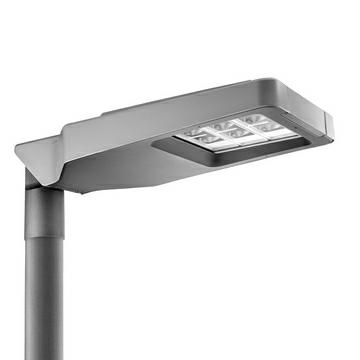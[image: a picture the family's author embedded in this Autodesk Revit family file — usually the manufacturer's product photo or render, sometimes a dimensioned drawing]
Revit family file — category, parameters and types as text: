
# Revit family: Lighting-StreetLighting-GEWISS-ROAD[5]MINI-LED_OPTIC_WIDE_CLII
name_source: partatom
category: Apparecchi per illuminazione
units: mm (PartAtom-declared; Revit-internal decimal feet)

## family parameters
Basato su piano di lavoro = No
Condiviso = No
Punto di calcolo locali = No
Quota connettore circolare = Usa diametro
Sempre verticale = Sì
Sorgente d'illuminazione = No
Taglio con vuoti quando caricato = No
Tipo di parte = Normale

## types (44) — shared parameters
Applicazione = External
Carico apparente = 53 VA
Catalogue = LIGHTING
Commenti sul wattaggio = 53W
IDF = 1914d6a6-8cfd-45a9-bf41-70975823a003
IDT = 3cb2f9b43b7a40689a44ddfc6caf9e96
IP degree = IP66
Immagine tipo = GWR5276M.jpg
Insulation class = II
Produttore = GEWISS S.p.A.
Shock resistance = IK08
Technical sheet = https://www.gewiss.com
URL = https://www.gewiss.com
Version file RFA = 20.11
Warranty = 5 years

## per-type parameters (varying)
- GWR5212V - ROAD5 MINI V.WIDE 2M 4000K 1,0A CL2: Body=Die-cast aluminium -; Catalogue Range=ROAD [5]; Classification:=-; Color Rendering Index=CRI-70; Colore=Graphite grey; Colour :=Powder coating; Colour temperature=4000K; Colour temperature:=4000 K (CRI>70); Context=Street and parking lighting; Control System=DALI - 5 Step; DIN 18032-3 certification=-; Descrizione=GWR5212V - ROAD5 MINI V.WIDE 2M 4000K 1,0A CL2; Device with reduced surface temperature=-; Driver=Included; Driver Box=Built-in; Efficiency (lm/W)=110; Electrocod=244C; Eletrical and lighting features=-; External screw=Stainless steel; Fixing=Pole Head - Outreach; Gasket=Anti-aging silicone; General information=-; Glow Wire Test :=-; IPEA=ROAD = A3 + // LARGE AREAS = A4 + // CYCLOPEDONALS = A ++ // GREEN AREAS = A ++ // HISTORICAL CENTER = A6 +; Installationa and maintenance=-; LED Life Time (L80B05)=120000H; LED Maintenance=Not available; LED current.=1A; Lamp-=LED; Lifetime=L90B10 (Tq+25°C) = 100.000 h - L90B10 (Tq+40°C) = 75.000 h; Locking Hook=Integrated front handle; Lumen output (lm)=8500; Luminaire=LED Road Equipment; Materials=-; Maximum surface exposed to the wind=0,149999999999999M2; Maximum surface exposed to the wind :=0.15 m²; Minimum distance from the illuminated object=1M; Modello=GWR5212V; Mouting and installation=Pole Head - Outreach; Nominal flux (lm)=9540; Number of modules=2 (2x3 LED); Operating temperature :=-25 +40 °C; Operating temperature:=-25 +40 °C; Optic=WIDE; Optic :=Metallized polycarbonate reflector; Optic Maintenance=Not available; Optic and illuminating features=-; Overvoltage protection=DM 10KV / CM 10KV; Photobiological Risk Class=RG0; Rated frequency (Hz)=50 / 60; SEO=Street lighting; Shield type=4mm thick flat tempered glass; Standard Deviation Colour Matching=SDCM = 5; Standard-=EN 60598-2-3, EN 60598-1 IEC/TR 62778; Standards and approvals=-; Stocking temperature=-; Supply voltage=220 - 240 V; System power=76W; System power :=77 W @ 1A; Tilt adjustable=-20° ÷ +10° side bracket - -10° ÷ +20° pole head; Tilt-=-20° ÷ +10° side bracket - -10° ÷ +20° pole head; Tipologia=Programmable (5 step); Type of light source=LED - Not replaceable; Unified Glare Rating=G*3 - ULOR = 0; Unique digital code (Datamatrix)=Currently not present; Voltage-=220/240 V - 50/60 Hz - Stand alone and/or programmable; Weight (kg):=6,6; Wiring=Isolating switch
- GWR5212B - ROAD 5 MINI BIPOW.2M 4000K 1A OPT.W: Catalogue Range=ROAD [5]; Colour temperature=4000 K (CRI 70); Colour temperature:=4000 K (CRI 70); Descrizione=ROAD 5 MINI BIPOW.2M 4000K 1A OPT.W; EAN code=8011564857872; Electrocod=244C; LED LifeTime (L80B05)=120000H; LED current.=1A; Lamp-=LED; Lumen output (lm)=7680; Maximum surface exposed to the wind=0,15M2; Minimum distance from the illuminated object=1M; Modello=GWR5212B; No. Chorus modules=2 (2x3 LED); Nominal flux (lm)=9540; Number of modules=2 (2x3 LED); Operating temperature:=-25 +40 °C; Optic=W - ULOR: 0%; Overvoltage resistance=12 KV (Common and dfferential mode); Pilot current=1A; Power supply operation=Bi power; SEO=Street lighting; System power=77W; Tilt adjustable=-20° ÷ +10° side bracket - -10° ÷ +20° pole head; Tipo alimentatore=Constant Current Driver Led; Tipologia=Bi power; Type of lamp=LED; Voltage-=220/240 V - 50/60 Hz - Bi-power with self-learning; Weight (kg)=6,6; Weight (kg):=6,6; Working temperature=-25 +40 °C
- GWR523130K - ROAD 5 MINI ST.AL.1M 3000K 350mA OPT.W: Body=Die-cast aluminium -; Catalogue Range=ROAD [5]; Classification:=-; Color Rendering Index=CRI-70; Colore=Graphite grey; Colour :=Powder coating; Colour temperature=3000K; Colour temperature:=3000 K (CRI>80); Context=Street and parking lighting; Control System=Stand alone; DIN 18032-3 certification=-; Descrizione=GWR523130K - ROAD 5 MINI ST.AL.1M 3000K 350mA OPT.W; Device with reduced surface temperature=-; Driver=Included; Driver Box=Built-in; Efficiency (lm/W)=115; Electrocod=244C; Eletrical and lighting features=-; External screw=Stainless steel; Fixing=Pole Head - Outreach; Gasket=Anti-aging silicone; General information=-; Glow Wire Test :=-; IPEA=ROAD = A4 + // LARGE AREAS = A5 + // CYCLOPEDONALS = A4 + // GREEN AREAS = A4 + // HISTORICAL CENTER = A6 +; Installationa and maintenance=-; LED Life Time (L80B05)=77000H; LED Maintenance=Not available; LED current.=0,35A; Lamp-=LED; Lifetime=L90B10 (Tq+25°C) = 100.000 h - L90B10 (Tq+50°C) = 75.000 h; Locking Hook=Integrated front handle; Lumen output (lm)=1500; Luminaire=LED Road Equipment; Materials=-; Maximum surface exposed to the wind=0,149999999999999M2; Maximum surface exposed to the wind :=0.15 m²; Minimum distance from the illuminated object=1M; Modello=GWR523130K; Mouting and installation=Pole Head - Outreach; Nominal flux (lm)=1350; Number of modules=1 (1x3 LED); Operating temperature :=-25 +50 °C; Operating temperature:=-25 +50 °C; Optic=WIDE; Optic :=Metallized polycarbonate reflector; Optic Maintenance=Not available; Optic and illuminating features=-; Overvoltage protection=DM 10KV / CM 10KV; Overvoltage resistance :=Common and dfferential mode: 10KV; Photobiological Risk Class=RG0; Rated frequency (Hz)=50 / 60; SEO=Street lighting; Shield type=4mm thick flat tempered glass; Standard Deviation Colour Matching=SDCM = 5; Standard-=EN 60598-2-3, EN 60598-1 IEC/TR 62778; Standards and approvals=-; Stocking temperature=-; Supply voltage=220 - 240 V; System power=14W; System power :=13 W @ 0.35A; Tilt adjustable=-20° ÷ +10° side bracket - -10° ÷ +20° pole head; Tilt-=-20° ÷ +10° side bracket - -10° ÷ +20° pole head; Tipo alimentatore=Constant Current Driver Led; Tipologia=Stand alone; Type of light source=LED - Not replaceable; Unified Glare Rating=G*3 - ULOR = 0; Unique digital code (Datamatrix)=Currently not present; Voltage-=220/240 V - 50/60 Hz - Stand alone; Weight (kg):=6,4; Wiring=Isolating switch
- GWR5212V30K - ROAD 5 MINI DIMM.2M 3000K 1A OPT.W: Body=Die-cast aluminium -; Classification:=-; Color Rendering Index=CRI-70; Colore=Graphite grey; Colour :=Powder coating; Colour temperature=3000K; Context=Street and parking lighting; Control System=DALI - 5 Step; DIN 18032-3 certification=-; Descrizione=GWR5212V30K - ROAD 5 MINI DIMM.2M 3000K 1A OPT.W; Device with reduced surface temperature=-; Driver=Included; Driver Box=Built-in; Efficiency (lm/W)=96; Eletrical and lighting features=-; External screw=Stainless steel; Fixing=Pole Head - Outreach; Gasket=Anti-aging silicone; General information=-; Glow Wire Test :=-; IPEA=ROAD = A + // LARGE AREAS = A ++ // CYCLOPEDONALS = A + // GREEN AREAS = A + // HISTORICAL CENTER = A5 +; Installationa and maintenance=-; LED Maintenance=Not available; Lifetime=L90B10 (Tq+25°C) = 100.000 h - L90B10 (Tq+40°C) = 75.000 h; Locking Hook=Integrated front handle; Lumen output (lm)=7400; Luminaire=LED Road Equipment; Materials=-; Maximum surface exposed to the wind :=0.15 m²; Modello=GWR5212V30K; Mouting and installation=Pole Head - Outreach; Number of modules=2 (2x3 LED); Operating temperature :=-25 +40 °C; Optic=WIDE; Optic :=Metallized polycarbonate reflector; Optic Maintenance=Not available; Optic and illuminating features=-; Overvoltage protection=DM 10KV / CM 10KV; Photobiological Risk Class=RG0; Rated frequency (Hz)=50 / 60; SEO=Street lighting; Shield type=4mm thick flat tempered glass; Standard Deviation Colour Matching=SDCM = 5; Standard-=EN 60598-2-3, EN 60598-1 IEC/TR 62778; Standards and approvals=-; Stocking temperature=-; Supply voltage=220 - 240 V; System power :=77 W @ 1A; Tilt-=-20° ÷ +10° side bracket - -10° ÷ +20° pole head; Type of light source=LED - Not replaceable; Unified Glare Rating=G*3 - ULOR = 0; Unique digital code (Datamatrix)=Currently not present; Weight (kg):=6,59999999999999; Wiring=Isolating switch
- GWR5271M30K - ROAD5 MINI WIDE 1M 3000K 0,7A CL2 1-10V: Body=Die-cast aluminium -; Catalogue Range=ROAD [5]; Classification:=-; Color Rendering Index=CRI-70; Colore=Graphite grey; Colour :=Powder coating; Colour temperature=3000K; Colour temperature:=3000 K (CRI>80); Context=Street and parking lighting; Control System=Dimmable 1-10 V; DIN 18032-3 certification=-; Descrizione=GWR5271M30K - ROAD5 MINI WIDE 1M 3000K 0,7A CL2 1-10V; Device with reduced surface temperature=-; Driver=Included; Driver Box=Built-in; Efficiency (lm/W)=100; Electrocod=244C; Eletrical and lighting features=-; External screw=Stainless steel; Fixing=Pole Head - Outreach; Gasket=Anti-aging silicone; General information=-; Glow Wire Test :=-; IPEA=ROAD = A ++ // LARGE AREAS = A3 + // CYCLOPEDONALS = A ++ // GREEN AREAS = A ++ // HISTORICAL CENTER = A5 +; Installationa and maintenance=-; LED Life Time (L80B05)=77000H; LED Maintenance=Not available; LED current.=0,7A; Lamp-=LED; Lifetime=L90B10 (Tq+25°C) = 100.000 h - L90B10 (Tq+50°C) = 75.000 h; Locking Hook=Integrated front handle; Lumen output (lm)=2800; Luminaire=LED Road Equipment; Materials=-; Maximum surface exposed to the wind=0,149999999999999M2; Maximum surface exposed to the wind :=0.15 m²; Minimum distance from the illuminated object=1M; Modello=GWR5271M30K; Mouting and installation=Pole Head - Outreach; Nominal flux (lm)=2700; Number of modules=1 (1x3 LED); Operating temperature :=-25 +50 °C; Operating temperature:=-25 +50 °C; Optic=WIDE; Optic :=Metallized polycarbonate reflector; Optic Maintenance=Not available; Optic and illuminating features=-; Overvoltage protection=DM 10KV / CM 10KV; Overvoltage resistance :=Common and dfferential mode: 10KV; Photobiological Risk Class=RG0; Power supply operation=Dimmable; Rated frequency (Hz)=50 / 60; SEO=Street lighting; Shield type=4mm thick flat tempered glass; Standard Deviation Colour Matching=SDCM = 5; Standard-=EN 60598-2-3, EN 60598-1 IEC/TR 62778; Standards and approvals=-; Stocking temperature=-; Supply voltage=220 - 240 V; System power=27W; System power :=28 W @ 0.7A; Tilt adjustable=-20° ÷ +10° side bracket - -10° ÷ +20° pole head; Tilt-=-20° ÷ +10° side bracket - -10° ÷ +20° pole head; Tipo alimentatore=Constant Current Driver Led; Tipologia=Dimmable; Type of light source=LED - Not replaceable; Unified Glare Rating=G*3 - ULOR = 0; Unique digital code (Datamatrix)=Currently not present; Voltage-=220/240 V - 50/60 Hz - Dimmable 1-10 V; Weight (kg):=6,4; Wiring=Isolating switch
- GWR5231 - ROAD 5 MINI ST.AL.1M 4000K 350mA OPT.W: Catalogue Range=ROAD [5]; Colour temperature=4000 K (CRI 70); Colour temperature:=4000 K (CRI 70); Descrizione=ROAD 5 MINI ST.AL.1M 4000K 350mA OPT.W; EAN code=8011564870222; Electrocod=244C; LED LifeTime (L80B05)=77000H; LED current.=0,35A; Lamp-=LED; Lumen output (lm)=1310; Maximum surface exposed to the wind=0,15M2; Minimum distance from the illuminated object=1M; Modello=GWR5231; No. Chorus modules=1 (1x3 LED); Nominal flux (lm)=1560; Number of modules=1 (1x3 LED); Operating temperature:=-25 +50 °C; Optic=W - ULOR: 0%; Overvoltage resistance=12 KV (Common and dfferential mode); Pilot current=0,35A; SEO=Street lighting; System power=14W; Tilt adjustable=-20° ÷ +10° side bracket - -10° ÷ +20° pole head; Tipo alimentatore=Constant Current Driver Led; Tipologia=Stand alone; Type of lamp=LED; Voltage-=220/240 V - 50/60 Hz - Stand alone; Weight (kg)=6,4; Weight (kg):=6,4; Working temperature=-25 +50 °C
- GWR5272B30K - ROAD5 MINI WIDE 2M 3000K 0,7A CL2 BIREG: Body=Die-cast aluminium -; Catalogue Range=ROAD [5]; Classification:=-; Color Rendering Index=CRI-70; Colore=Graphite grey; Colour :=Powder coating; Colour temperature=3000K; Colour temperature:=3000 K (CRI>80); Context=Street and parking lighting; Control System=Bi-power with self-learning; DIN 18032-3 certification=-; Descrizione=GWR5272B30K - ROAD5 MINI WIDE 2M 3000K 0,7A CL2 BIREG; Device with reduced surface temperature=-; Driver=Included; Driver Box=Built-in; Efficiency (lm/W)=102; Electrocod=244C; Eletrical and lighting features=-; External screw=Stainless steel; Fixing=Pole Head - Outreach; Gasket=Anti-aging silicone; General information=-; Glow Wire Test :=-; IPEA=ROAD = A ++ // LARGE AREAS = A3 + // CYCLOPEDONALS = A ++ // GREEN AREAS = A ++ // HISTORICAL CENTER = A5 +; Installationa and maintenance=-; LED Life Time (L80B05)=77000H; LED Maintenance=Not available; LED current.=0,7A; Lamp-=LED; Lifetime=L90B10 (Tq+25°C) = 100.000 h - L90B10 (Tq+50°C) = 75.000 h; Locking Hook=Integrated front handle; Lumen output (lm)=5500; Luminaire=LED Road Equipment; Materials=-; Maximum surface exposed to the wind=0,149999999999999M2; Maximum surface exposed to the wind :=0.15 m²; Minimum distance from the illuminated object=1M; Modello=GWR5272B30K; Mouting and installation=Pole Head - Outreach; Nominal flux (lm)=5400; Number of modules=2 (2x3 LED); Operating temperature :=-25 +50 °C; Operating temperature:=-25 +50 °C; Optic=WIDE; Optic :=Metallized polycarbonate reflector; Optic Maintenance=Not available; Optic and illuminating features=-; Overvoltage protection=DM 10KV / CM 10KV; Overvoltage resistance :=Common and dfferential mode: 10KV; Photobiological Risk Class=RG0; Power supply operation=Bi power; Rated frequency (Hz)=50 / 60; SEO=Street lighting; Shield type=4mm thick flat tempered glass; Standard Deviation Colour Matching=SDCM = 5; Standard-=EN 60598-2-3, EN 60598-1 IEC/TR 62778; Standards and approvals=-; Stocking temperature=-; Supply voltage=220 - 240 V; System power=54W; System power :=54 W @ 0.7A; Tilt adjustable=-20° ÷ +10° side bracket - -10° ÷ +20° pole head; Tilt-=-20° ÷ +10° side bracket - -10° ÷ +20° pole head; Tipo alimentatore=Constant Current Driver Led; Tipologia=Bi power; Type of light source=LED - Not replaceable; Unified Glare Rating=G*3 - ULOR = 0; Unique digital code (Datamatrix)=Currently not present; Voltage-=220/240 V - 50/60 Hz - Bi-power with self-learning; Weight (kg):=6,6; Wiring=Isolating switch
- GWR527230K - ROAD 5 MINI ST.AL.2M 3000K 700mA OPT.W: Body=Die-cast aluminium -; Catalogue Range=ROAD [5]; Classification:=-; Color Rendering Index=CRI-70; Colore=Graphite grey; Colour :=Powder coating; Colour temperature=3000K; Colour temperature:=3000 K (CRI>80); Context=Street and parking lighting; Control System=Stand alone; DIN 18032-3 certification=-; Descrizione=GWR527230K - ROAD 5 MINI ST.AL.2M 3000K 700mA OPT.W; Device with reduced surface temperature=-; Driver=Included; Driver Box=Built-in; Efficiency (lm/W)=104; Electrocod=244C; Eletrical and lighting features=-; External screw=Stainless steel; Fixing=Pole Head - Outreach; Gasket=Anti-aging silicone; General information=-; Glow Wire Test :=-; IPEA=ROAD = A3 + // LARGE AREAS = A3 + // CYCLOPEDONALS = A ++ // GREEN AREAS = A ++ // HISTORICAL CENTER = A6 +; Installationa and maintenance=-; LED Life Time (L80B05)=77000H; LED Maintenance=Not available; LED current.=0,7A; Lamp-=LED; Lifetime=L90B10 (Tq+25°C) = 100.000 h - L90B10 (Tq+50°C) = 75.000 h; Locking Hook=Integrated front handle; Lumen output (lm)=5500; Luminaire=LED Road Equipment; Materials=-; Maximum surface exposed to the wind=0,149999999999999M2; Maximum surface exposed to the wind :=0.15 m²; Minimum distance from the illuminated object=1M; Modello=GWR527230K; Mouting and installation=Pole Head - Outreach; Nominal flux (lm)=5400; Number of modules=2 (2x3 LED); Operating temperature :=-25 +50 °C; Operating temperature:=-25 +50 °C; Optic=WIDE; Optic :=Metallized polycarbonate reflector; Optic Maintenance=Not available; Optic and illuminating features=-; Overvoltage protection=DM 10KV / CM 10KV; Overvoltage resistance :=Common and dfferential mode: 10KV; Photobiological Risk Class=RG0; Rated frequency (Hz)=50 / 60; SEO=Street lighting; Shield type=4mm thick flat tempered glass; Standard Deviation Colour Matching=SDCM = 5; Standard-=EN 60598-2-3, EN 60598-1 IEC/TR 62778; Standards and approvals=-; Stocking temperature=-; Supply voltage=220 - 240 V; System power=53W; System power :=53 W @ 0.7A; Tilt adjustable=-20° ÷ +10° side bracket - -10° ÷ +20° pole head; Tilt-=-20° ÷ +10° side bracket - -10° ÷ +20° pole head; Tipo alimentatore=Constant Current Driver Led; Tipologia=Stand alone; Type of light source=LED - Not replaceable; Unified Glare Rating=G*3 - ULOR = 0; Unique digital code (Datamatrix)=Currently not present; Voltage-=220/240 V - 50/60 Hz - Stand alone; Weight (kg):=6,6; Wiring=Isolating switch
- GWR5252M30K - ROAD5 MINI WIDE 2M 3000K 0,50A CL2: Body=Die-cast aluminium -; Classification:=-; Color Rendering Index=CRI-70; Colore=Graphite grey; Colour :=Powder coating; Colour temperature=3000K; Context=Street and parking lighting; Control System=Dimmable 1-10 V; DIN 18032-3 certification=-; Descrizione=GWR5252M30K - ROAD5 MINI WIDE 2M 3000K 0,50A CL2; Device with reduced surface temperature=-; Driver=Included; Driver Box=Built-in; Efficiency (lm/W)=108; Eletrical and lighting features=-; External screw=Stainless steel; Fixing=Pole Head - Outreach; Gasket=Anti-aging silicone; General information=-; Glow Wire Test :=-; IPEA=ROAD = A3 + // LARGE AREAS = A4 + // CYCLOPEDONALS = A3 + // GREEN AREAS = A3 + // HISTORICAL CENTER = A6 +; Installationa and maintenance=-; LED Maintenance=Not available; Lifetime=L90B10 (Tq+25°C) = 100.000 h - L90B10 (Tq+50°C) = 75.000 h; Locking Hook=Integrated front handle; Lumen output (lm)=4100; Luminaire=LED Road Equipment; Materials=-; Maximum surface exposed to the wind :=0.15 m²; Modello=GWR5252M30K; Mouting and installation=Pole Head - Outreach; Number of modules=2 (2x3 LED); Operating temperature :=-25 +50 °C; Optic=WIDE; Optic :=Metallized polycarbonate reflector; Optic Maintenance=Not available; Optic and illuminating features=-; Overvoltage protection=DM 10KV / CM 10KV; Photobiological Risk Class=RG0; Rated frequency (Hz)=50 / 60; SEO=Street lighting; Shield type=4mm thick flat tempered glass; Standard Deviation Colour Matching=SDCM = 5; Standard-=EN 60598-2-3, EN 60598-1 IEC/TR 62778; Standards and approvals=-; Stocking temperature=-; Supply voltage=220 - 240 V; System power :=38 W @ 0.5A; Tilt-=-20° ÷ +10° side bracket - -10° ÷ +20° pole head; Type of light source=LED - Not replaceable; Unified Glare Rating=G*3 - ULOR = 0; Unique digital code (Datamatrix)=Currently not present; Weight (kg):=6,59999999999999; Wiring=Isolating switch
- GWR5251D30K - ROAD5 MINI WIDE 1M 3000K 0,5A CL2 DALI: Body=Die-cast aluminium -; Classification:=-; Color Rendering Index=CRI-70; Colore=Graphite grey; Colour :=Powder coating; Colour temperature=3000K; Context=Street and parking lighting; Control System=DALI; DIN 18032-3 certification=-; Descrizione=GWR5251D30K - ROAD5 MINI WIDE 1M 3000K 0,5A CL2 DALI; Device with reduced surface temperature=-; Driver=Included; Driver Box=Built-in; Efficiency (lm/W)=105; Eletrical and lighting features=-; External screw=Stainless steel; Fixing=Pole Head - Outreach; Gasket=Anti-aging silicone; General information=-; Glow Wire Test :=-; IPEA=ROAD = A3 + // LARGE AREAS = A3 + // CYCLOPEDONALS = A3 + // GREEN AREAS = A3 + // HISTORICAL CENTER = A6 +; Installationa and maintenance=-; LED Maintenance=Not available; Lifetime=L90B10 (Tq+25°C) = 100.000 h - L90B10 (Tq+50°C) = 75.000 h; Locking Hook=Integrated front handle; Lumen output (lm)=2100; Luminaire=LED Road Equipment; Materials=-; Maximum surface exposed to the wind :=0.15 m²; Modello=GWR5251D30K; Mouting and installation=Pole Head - Outreach; Number of modules=1 (1x3 LED); Operating temperature :=-25 +50 °C; Optic=WIDE; Optic :=Metallized polycarbonate reflector; Optic Maintenance=Not available; Optic and illuminating features=-; Overvoltage protection=DM 10KV / CM 10KV; Photobiological Risk Class=RG0; Rated frequency (Hz)=50 / 60; Shield type=4mm thick flat tempered glass; Standard Deviation Colour Matching=SDCM = 5; Standard-=EN 60598-2-3, EN 60598-1 IEC/TR 62778; Standards and approvals=-; Stocking temperature=-; Supply voltage=220 - 240 V; System power :=20 W @ 0.5A; Tilt-=-20° ÷ +10° side bracket - -10° ÷ +20° pole head; Type of light source=LED - Not replaceable; Unified Glare Rating=G*3 - ULOR = 0; Unique digital code (Datamatrix)=Currently not present; Weight (kg):=6,4; Wiring=Isolating switch
- GWR5231V - ROAD5 MINI V.WIDE 1M 4000K 0,35A CL2: Body=Die-cast aluminium -; Catalogue Range=ROAD [5]; Classification:=-; Color Rendering Index=CRI-70; Colore=Graphite grey; Colour :=Powder coating; Colour temperature=4000K; Colour temperature:=4000 K (CRI>70); Context=Street and parking lighting; Control System=DALI - 5 Step; DIN 18032-3 certification=-; Descrizione=GWR5231V - ROAD5 MINI V.WIDE 1M 4000K 0,35A CL2; Device with reduced surface temperature=-; Driver=Included; Driver Box=Built-in; Efficiency (lm/W)=121; Electrocod=244C; Eletrical and lighting features=-; External screw=Stainless steel; Fixing=Pole Head - Outreach; Gasket=Anti-aging silicone; General information=-; Glow Wire Test :=-; IPEA=ROAD = A5 + // LARGE AREAS = A6 + // CYCLOPEDONALS = A5 + // GREEN AREAS = A5 + // HISTORICAL CENTER = A6 +; Installationa and maintenance=-; LED Life Time (L80B05)=120000H; LED Maintenance=Not available; LED current.=0,35A; Lamp-=LED; Lifetime=L90B10 (Tq+25°C) = 100.000 h - L90B10 (Tq+50°C) = 75.000 h; Locking Hook=Integrated front handle; Lumen output (lm)=1700; Luminaire=LED Road Equipment; Materials=-; Maximum surface exposed to the wind=0,149999999999999M2; Maximum surface exposed to the wind :=0.15 m²; Minimum distance from the illuminated object=1M; Modello=GWR5231V; Mouting and installation=Pole Head - Outreach; Nominal flux (lm)=1560; Number of modules=1 (1x3 LED); Operating temperature :=-25 +50 °C; Operating temperature:=-25 +40 °C; Optic=WIDE; Optic :=Metallized polycarbonate reflector; Optic Maintenance=Not available; Optic and illuminating features=-; Overvoltage protection=DM 10KV / CM 10KV; Photobiological Risk Class=RG0; Rated frequency (Hz)=50 / 60; SEO=Street lighting; Shield type=4mm thick flat tempered glass; Standard Deviation Colour Matching=SDCM = 5; Standard-=EN 60598-2-3, EN 60598-1 IEC/TR 62778; Standards and approvals=-; Stocking temperature=-; Supply voltage=220 - 240 V; System power=14W; System power :=14 W @ 0.35A; Tilt adjustable=-20° ÷ +10° side bracket - -10° ÷ +20° pole head; Tilt-=-20° ÷ +10° side bracket - -10° ÷ +20° pole head; Tipologia=Programmable (5 step); Type of light source=LED - Not replaceable; Unified Glare Rating=G*3 - ULOR = 0; Unique digital code (Datamatrix)=Currently not present; Voltage-=220/240 V - 50/60 Hz - Stand alone and/or programmable; Weight (kg):=6,4; Wiring=Isolating switch
- GWR5212D30K - ROAD5 MINI WIDE 2M 3000K 1,0A CL2 DALI: Body=Die-cast aluminium -; Classification:=-; Color Rendering Index=CRI-70; Colore=Graphite grey; Colour :=Powder coating; Colour temperature=3000K; Context=Street and parking lighting; Control System=DALI; DIN 18032-3 certification=-; Descrizione=GWR5212D30K - ROAD5 MINI WIDE 2M 3000K 1,0A CL2 DALI; Device with reduced surface temperature=-; Driver=Included; Driver Box=Built-in; Efficiency (lm/W)=96; Eletrical and lighting features=-; External screw=Stainless steel; Fixing=Pole Head - Outreach; Gasket=Anti-aging silicone; General information=-; Glow Wire Test :=-; IPEA=ROAD = A + // LARGE AREAS = A ++ // CYCLOPEDONALS = A + // GREEN AREAS = A + // HISTORICAL CENTER = A5 +; Installationa and maintenance=-; LED Maintenance=Not available; Lifetime=L90B10 (Tq+25°C) = 100.000 h - L90B10 (Tq+40°C) = 75.000 h; Locking Hook=Integrated front handle; Lumen output (lm)=7400; Luminaire=LED Road Equipment; Materials=-; Maximum surface exposed to the wind :=0.15 m²; Modello=GWR5212D30K; Mouting and installation=Pole Head - Outreach; Number of modules=2 (2x3 LED); Operating temperature :=-25 +40 °C; Optic=WIDE; Optic :=Metallized polycarbonate reflector; Optic Maintenance=Not available; Optic and illuminating features=-; Overvoltage protection=DM 10KV / CM 10KV; Photobiological Risk Class=RG0; Rated frequency (Hz)=50 / 60; Shield type=4mm thick flat tempered glass; Standard Deviation Colour Matching=SDCM = 5; Standard-=EN 60598-2-3, EN 60598-1 IEC/TR 62778; Standards and approvals=-; Stocking temperature=-; Supply voltage=220 - 240 V; System power :=77 W @ 1A; Tilt-=-20° ÷ +10° side bracket - -10° ÷ +20° pole head; Type of light source=LED - Not replaceable; Unified Glare Rating=G*3 - ULOR = 0; Unique digital code (Datamatrix)=Currently not present; Weight (kg):=6,59999999999999; Wiring=Isolating switch
- GWR5211 - ROAD 5 MINI ST.AL.1M 4000K 1A OPT.W: Catalogue Range=ROAD [5]; Colour temperature=4000 K (CRI 70); Colour temperature:=4000 K (CRI 70); Descrizione=ROAD 5 MINI ST.AL.1M 4000K 1A OPT.W; EAN code=8011564857810; Electrocod=244C; LED LifeTime (L80B05)=120000H; LED current.=1A; Lamp-=LED; Lumen output (lm)=3840; Maximum surface exposed to the wind=0,15M2; Minimum distance from the illuminated object=1M; Modello=GWR5211; No. Chorus modules=1 (1x3 LED); Nominal flux (lm)=4770; Number of modules=1 (1x3 LED); Operating temperature:=-25 +40 °C; Optic=W - ULOR: 0%; Overvoltage resistance=12 KV (Common and dfferential mode); Pilot current=1A; SEO=Street lighting; System power=38W; Tilt adjustable=-20° ÷ +10° side bracket - -10° ÷ +20° pole head; Tipo alimentatore=Constant Current Driver Led; Tipologia=Stand alone; Type of lamp=LED; Voltage-=220/240 V - 50/60 Hz - Stand alone; Weight (kg)=6,4; Weight (kg):=6,4; Working temperature=-25 +40 °C
- GWR5272 - ROAD 5 MINI ST.AL.2M 4000K 700mA OPT.W: Catalogue Range=ROAD [5]; Colour temperature=4000 K (CRI 70); Colour temperature:=4000 K (CRI 70); Descrizione=ROAD 5 MINI ST.AL.2M 4000K 700mA OPT.W; EAN code=8011564857827; Electrocod=244C; LED LifeTime (L80B05)=77000H; LED current.=0,7A; Lamp-=LED; Lumen output (lm)=5240; Maximum surface exposed to the wind=0,15M2; Minimum distance from the illuminated object=1M; Modello=GWR5272; No. Chorus modules=2 (2x3 LED); Nominal flux (lm)=6240; Number of modules=2 (2x3 LED); Operating temperature:=-25 +50 °C; Optic=W - ULOR: 0%; Overvoltage resistance=12 KV (Common and dfferential mode); Pilot current=0,7A; SEO=Street lighting; System power=53W; Tilt adjustable=-20° ÷ +10° side bracket - -10° ÷ +20° pole head; Tipo alimentatore=Constant Current Driver Led; Tipologia=Stand alone; Type of lamp=LED; Voltage-=220/240 V - 50/60 Hz - Stand alone; Weight (kg)=6,6; Weight (kg):=6,6; Working temperature=-25 +50 °C
- GWR5212B30K - ROAD5 MINI WIDE 2M 3000K 1,0A CL2 BIREG: Body=Die-cast aluminium -; Catalogue Range=ROAD [5]; Classification:=-; Color Rendering Index=CRI-70; Colore=Graphite grey; Colour :=Powder coating; Colour temperature=3000K; Colour temperature:=3000 K (CRI>80); Context=Street and parking lighting; Control System=Bi-power with self-learning; DIN 18032-3 certification=-; Descrizione=GWR5212B30K - ROAD5 MINI WIDE 2M 3000K 1,0A CL2 BIREG; Device with reduced surface temperature=-; Driver=Included; Driver Box=Built-in; Efficiency (lm/W)=96; Electrocod=244C; Eletrical and lighting features=-; External screw=Stainless steel; Fixing=Pole Head - Outreach; Gasket=Anti-aging silicone; General information=-; Glow Wire Test :=-; IPEA=ROAD = A + // LARGE AREAS = A ++ // CYCLOPEDONALS = A + // GREEN AREAS = A + // HISTORICAL CENTER = A5 +; Installationa and maintenance=-; LED Life Time (L80B05)=120000H; LED Maintenance=Not available; LED current.=1A; Lamp-=LED; Lifetime=L90B10 (Tq+25°C) = 100.000 h - L90B10 (Tq+40°C) = 75.000 h; Locking Hook=Integrated front handle; Lumen output (lm)=7400; Luminaire=LED Road Equipment; Materials=-; Maximum surface exposed to the wind=0,149999999999999M2; Maximum surface exposed to the wind :=0.15 m²; Minimum distance from the illuminated object=1M; Modello=GWR5212B30K; Mouting and installation=Pole Head - Outreach; Nominal flux (lm)=8280; Number of modules=2 (2x3 LED); Operating temperature :=-25 +40 °C; Operating temperature:=-25 +40 °C; Optic=WIDE; Optic :=Metallized polycarbonate reflector; Optic Maintenance=Not available; Optic and illuminating features=-; Overvoltage protection=DM 10KV / CM 10KV; Overvoltage resistance :=Common and dfferential mode: 10KV; Photobiological Risk Class=RG0; Power supply operation=Bi power; Rated frequency (Hz)=50 / 60; SEO=Street lighting; Shield type=4mm thick flat tempered glass; Standard Deviation Colour Matching=SDCM = 5; Standard-=EN 60598-2-3, EN 60598-1 IEC/TR 62778; Standards and approvals=-; Stocking temperature=-; Supply voltage=220 - 240 V; System power=77W; System power :=77 W @ 1A; Tilt adjustable=-20° ÷ +10° side bracket - -10° ÷ +20° pole head; Tilt-=-20° ÷ +10° side bracket - -10° ÷ +20° pole head; Tipo alimentatore=Constant Current Driver Led; Tipologia=Bi power; Type of light source=LED - Not replaceable; Unified Glare Rating=G*3 - ULOR = 0; Unique digital code (Datamatrix)=Currently not present; Voltage-=220/240 V - 50/60 Hz - Bi-power with self-learning; Weight (kg):=6,6; Wiring=Isolating switch
- GWR5271M - ROAD5 MINI WIDE 1M 4000K 0,7A CL2 1-10V: Catalogue Range=ROAD [5]; Colour temperature=4000 K (CRI 70); Colour temperature:=4000 K (CRI 70); Descrizione=ROAD 5 MINI DIMM.1M 4000K 700mA OPT.W; EAN code=8011564857889; Electrocod=244C; LED LifeTime (L80B05)=77000H; LED current.=0,7A; Lamp-=LED; Lumen output (lm)=2620; Maximum surface exposed to the wind=0,15M2; Minimum distance from the illuminated object=1M; Modello=GWR5271M; No. Chorus modules=1 (1x3 LED); Nominal flux (lm)=3120; Number of modules=1 (1x3 LED); Operating temperature:=-25 +50 °C; Optic=W - ULOR: 0%; Overvoltage resistance=12 KV (Common and dfferential mode); Pilot current=0,7A; Power supply operation=Dimmable; SEO=Street lighting; System power=27W; Tilt adjustable=-20° ÷ +10° side bracket - -10° ÷ +20° pole head; Tipo alimentatore=Constant Current Driver Led; Tipologia=Dimmable; Type of lamp=LED; Voltage-=220/240 V - 50/60 Hz - Dimmable 1-10 V; Weight (kg)=6,4; Weight (kg):=6,4; Working temperature=-25 +50 °C
- GWR5212 - ROAD 5 MINI ST.AL.2M 4000K 1A OPT.W: Catalogue Range=ROAD [5]; Colour temperature=4000 K (CRI 70); Colour temperature:=4000 K (CRI 70); Descrizione=ROAD 5 MINI ST.AL.2M 4000K 1A OPT.W; EAN code=8011564857834; Electrocod=244C; LED LifeTime (L80B05)=120000H; LED current.=1A; Lamp-=LED; Lumen output (lm)=7680; Maximum surface exposed to the wind=0,15M2; Minimum distance from the illuminated object=1M; Modello=GWR5212; No. Chorus modules=2 (2x3 LED); Nominal flux (lm)=9540; Number of modules=2 (2x3 LED); Operating temperature:=-25 +40 °C; Optic=W - ULOR: 0%; Overvoltage resistance=12 KV (Common and dfferential mode); Pilot current=1A; SEO=Street lighting; System power=76W; Tilt adjustable=-20° ÷ +10° side bracket - -10° ÷ +20° pole head; Tipo alimentatore=Constant Current Driver Led; Tipologia=Stand alone; Type of lamp=LED; Voltage-=220/240 V - 50/60 Hz - Stand alone; Weight (kg)=6,6; Weight (kg):=6,6; Working temperature=-25 +40 °C
- GWR5211B30K - ROAD5 MINI WIDE 1M 3000K 1,0A CL2 BIREG: Body=Die-cast aluminium -; Catalogue Range=ROAD [5]; Classification:=-; Color Rendering Index=CRI-70; Colore=Graphite grey; Colour :=Powder coating; Colour temperature=3000K; Colour temperature:=3000 K (CRI>80); Context=Street and parking lighting; Control System=Bi-power with self-learning; DIN 18032-3 certification=-; Descrizione=GWR5211B30K - ROAD5 MINI WIDE 1M 3000K 1,0A CL2 BIREG; Device with reduced surface temperature=-; Driver=Included; Driver Box=Built-in; Efficiency (lm/W)=95; Electrocod=244C; Eletrical and lighting features=-; External screw=Stainless steel; Fixing=Pole Head - Outreach; Gasket=Anti-aging silicone; General information=-; Glow Wire Test :=-; IPEA=ROAD = A + // LARGE AREAS = A ++ // CYCLOPEDONALS = A + // GREEN AREAS = A + // HISTORICAL CENTER = A4 +; Installationa and maintenance=-; LED Life Time (L80B05)=120000H; LED Maintenance=Not available; LED current.=1A; Lamp-=LED; Lifetime=L90B10 (Tq+25°C) = 100.000 h - L90B10 (Tq+40°C) = 75.000 h; Locking Hook=Integrated front handle; Lumen output (lm)=3700; Luminaire=LED Road Equipment; Materials=-; Maximum surface exposed to the wind=0,149999999999999M2; Maximum surface exposed to the wind :=0.15 m²; Minimum distance from the illuminated object=1M; Modello=GWR5211B30K; Mouting and installation=Pole Head - Outreach; Nominal flux (lm)=4140; Number of modules=1 (1x3 LED); Operating temperature :=-25 +40 °C; Operating temperature:=-25 +40 °C; Optic=WIDE; Optic :=Metallized polycarbonate reflector; Optic Maintenance=Not available; Optic and illuminating features=-; Overvoltage protection=DM 10KV / CM 10KV; Overvoltage resistance :=Common and dfferential mode: 10KV; Photobiological Risk Class=RG0; Power supply operation=Bi power; Rated frequency (Hz)=50 / 60; SEO=Street lighting; Shield type=4mm thick flat tempered glass; Standard Deviation Colour Matching=SDCM = 5; Standard-=EN 60598-2-3, EN 60598-1 IEC/TR 62778; Standards and approvals=-; Stocking temperature=-; Supply voltage=220 - 240 V; System power=39W; System power :=39 W @ 1A; Tilt adjustable=-20° ÷ +10° side bracket - -10° ÷ +20° pole head; Tilt-=-20° ÷ +10° side bracket - -10° ÷ +20° pole head; Tipo alimentatore=Constant Current Driver Led; Tipologia=Bi power; Type of light source=LED - Not replaceable; Unified Glare Rating=G*3 - ULOR = 0; Unique digital code (Datamatrix)=Currently not present; Voltage-=220/240 V - 50/60 Hz - Bi-power with self-learning; Weight (kg):=6,4; Wiring=Isolating switch
- GWR5211B - ROAD 5 MINI BIPOW.1M 4000K 1A OPT.W: Catalogue Range=ROAD [5]; Colour temperature=4000 K (CRI 70); Colour temperature:=4000 K (CRI 70); Descrizione=ROAD 5 MINI BIPOW.1M 4000K 1A OPT.W; EAN code=8011564857858; Electrocod=244C; LED LifeTime (L80B05)=120000H; LED current.=1A; Lamp-=LED; Lumen output (lm)=3840; Maximum surface exposed to the wind=0,15M2; Minimum distance from the illuminated object=1M; Modello=GWR5211B; No. Chorus modules=1 (1x3 LED); Nominal flux (lm)=4770; Number of modules=1 (1x3 LED); Operating temperature:=-25 +40 °C; Optic=W - ULOR: 0%; Overvoltage resistance=12 KV (Common and dfferential mode); Pilot current=1A; Power supply operation=Bi power; SEO=Street lighting; System power=39W; Tilt adjustable=-20° ÷ +10° side bracket - -10° ÷ +20° pole head; Tipo alimentatore=Constant Current Driver Led; Tipologia=Bi power; Type of lamp=LED; Voltage-=220/240 V - 50/60 Hz - Bi-power with self-learning; Weight (kg)=6,4; Weight (kg):=6,4; Working temperature=-25 +40 °C
- GWR5271V - ROAD5 MINI V.WIDE 1M 4000K 0,7A CL2: Body=Die-cast aluminium -; Catalogue Range=ROAD [5]; Classification:=-; Color Rendering Index=CRI-70; Colore=Graphite grey; Colour :=Powder coating; Colour temperature=4000K; Colour temperature:=4000 K (CRI>70); Context=Street and parking lighting; Control System=DALI - 5 Step; DIN 18032-3 certification=-; Descrizione=GWR5271V - ROAD5 MINI V.WIDE 1M 4000K 0,7A CL2; Device with reduced surface temperature=-; Driver=Included; Driver Box=Built-in; Efficiency (lm/W)=114; Electrocod=244C; Eletrical and lighting features=-; External screw=Stainless steel; Fixing=Pole Head - Outreach; Gasket=Anti-aging silicone; General information=-; Glow Wire Test :=-; IPEA=ROAD = A4 + // LARGE AREAS = A5 + // CYCLOPEDONALS = A4 + // GREEN AREAS = A4 + // HISTORICAL CENTER = A6 +; Installationa and maintenance=-; LED Life Time (L80B05)=120000H; LED Maintenance=Not available; LED current.=0,7A; Lamp-=LED; Lifetime=L90B10 (Tq+25°C) = 100.000 h - L90B10 (Tq+50°C) = 75.000 h; Locking Hook=Integrated front handle; Lumen output (lm)=3200; Luminaire=LED Road Equipment; Materials=-; Maximum surface exposed to the wind=0,149999999999999M2; Maximum surface exposed to the wind :=0.15 m²; Minimum distance from the illuminated object=1M; Modello=GWR5271V; Mouting and installation=Pole Head - Outreach; Nominal flux (lm)=3120; Number of modules=1 (1x3 LED); Operating temperature :=-25 +50 °C; Operating temperature:=-25 +40 °C; Optic=WIDE; Optic :=Metallized polycarbonate reflector; Optic Maintenance=Not available; Optic and illuminating features=-; Overvoltage protection=DM 10KV / CM 10KV; Photobiological Risk Class=RG0; Rated frequency (Hz)=50 / 60; SEO=Street lighting; Shield type=4mm thick flat tempered glass; Standard Deviation Colour Matching=SDCM = 5; Standard-=EN 60598-2-3, EN 60598-1 IEC/TR 62778; Standards and approvals=-; Stocking temperature=-; Supply voltage=220 - 240 V; System power=27W; System power :=28 W @ 0.7A; Tilt adjustable=-20° ÷ +10° side bracket - -10° ÷ +20° pole head; Tilt-=-20° ÷ +10° side bracket - -10° ÷ +20° pole head; Tipologia=Programmable (5 step); Type of light source=LED - Not replaceable; Unified Glare Rating=G*3 - ULOR = 0; Unique digital code (Datamatrix)=Currently not present; Voltage-=220/240 V - 50/60 Hz - Stand alone and/or programmable; Weight (kg):=6,4; Wiring=Isolating switch
- GWR5252B - ROAD5 MINI WIDE 2M 4000K 0,5A CL2 BIREG: Body=Die-cast aluminium -; Catalogue Range=ROAD [5]; Classification:=-; Color Rendering Index=CRI-70; Colore=Graphite grey; Colour :=Powder coating; Colour temperature=4000K; Colour temperature:=4000 K (CRI>70); Context=Street and parking lighting; Control System=Bi-power with self-learning; DIN 18032-3 certification=-; Descrizione=GWR5252B - ROAD5 MINI WIDE 2M 4000K 0,5A CL2 BIREG; Device with reduced surface temperature=-; Driver=Included; Driver Box=Built-in; Efficiency (lm/W)=124; Electrocod=244C; Eletrical and lighting features=-; External screw=Stainless steel; Fixing=Pole Head - Outreach; Gasket=Anti-aging silicone; General information=-; Glow Wire Test :=-; IPEA=ROAD = A5 + // LARGE AREAS = A6 + // CYCLOPEDONALS = A5 + // GREEN AREAS = A5 + // HISTORICAL CENTER = A6 +; Installationa and maintenance=-; LED Life Time (L80B05)=120000H; LED Maintenance=Not available; LED current.=0,5A; Lamp-=LED; Lifetime=L90B10 (Tq+25°C) = 100.000 h - L90B10 (Tq+50°C) = 75.000 h; Locking Hook=Integrated front handle; Lumen output (lm)=4700; Luminaire=LED Road Equipment; Materials=-; Maximum surface exposed to the wind=0,149999999999999M2; Maximum surface exposed to the wind :=0.15 m²; Minimum distance from the illuminated object=1M; Modello=GWR5252B; Mouting and installation=Pole Head - Outreach; Nominal flux (lm)=4800; Number of modules=2 (2x3 LED); Operating temperature :=-25 +50 °C; Operating temperature:=-25 +40 °C; Optic=WIDE; Optic :=Metallized polycarbonate reflector; Optic Maintenance=Not available; Optic and illuminating features=-; Overvoltage protection=DM 10KV / CM 10KV; Photobiological Risk Class=RG0; Power supply operation=Bi power; Rated frequency (Hz)=50 / 60; SEO=Street lighting; Shield type=4mm thick flat tempered glass; Standard Deviation Colour Matching=SDCM = 5; Standard-=EN 60598-2-3, EN 60598-1 IEC/TR 62778; Standards and approvals=-; Stocking temperature=-; Supply voltage=220 - 240 V; System power=36W; System power :=38 W @ 0.5A; Tilt adjustable=-20° ÷ +10° side bracket - -10° ÷ +20° pole head; Tilt-=-20° ÷ +10° side bracket - -10° ÷ +20° pole head; Type of light source=LED - Not replaceable; Unified Glare Rating=G*3 - ULOR = 0; Unique digital code (Datamatrix)=Currently not present; Voltage-=220/240 V - 50/60 Hz - Bi-power with self-learning; Weight (kg):=6,6; Wiring=Isolating switch
- GWR5252M - ROAD5 MINI WIDE 2M 4000K 0,5A CL2 1-10V: Body=Die-cast aluminium -; Catalogue Range=ROAD [5]; Classification:=-; Color Rendering Index=CRI-70; Colore=Graphite grey; Colour :=Powder coating; Colour temperature=4000K; Colour temperature:=4000 K (CRI>70); Context=Street and parking lighting; Control System=Dimmable 1-10 V; DIN 18032-3 certification=-; Descrizione=GWR5252M - ROAD5 MINI WIDE 2M 4000K 0,5A CL2 1-10V; Device with reduced surface temperature=-; Driver=Included; Driver Box=Built-in; Efficiency (lm/W)=124; Electrocod=244C; Eletrical and lighting features=-; External screw=Stainless steel; Fixing=Pole Head - Outreach; Gasket=Anti-aging silicone; General information=-; Glow Wire Test :=-; IPEA=ROAD = A5 + // LARGE AREAS = A6 + // CYCLOPEDONALS = A5 + // GREEN AREAS = A5 + // HISTORICAL CENTER = A6 +; Installationa and maintenance=-; LED Life Time (L80B05)=120000H; LED Maintenance=Not available; LED current.=0,5A; Lamp-=LED; Lifetime=L90B10 (Tq+25°C) = 100.000 h - L90B10 (Tq+50°C) = 75.000 h; Locking Hook=Integrated front handle; Lumen output (lm)=4700; Luminaire=LED Road Equipment; Materials=-; Maximum surface exposed to the wind=0,149999999999999M2; Maximum surface exposed to the wind :=0.15 m²; Minimum distance from the illuminated object=1M; Modello=GWR5252M; Mouting and installation=Pole Head - Outreach; Nominal flux (lm)=4800; Number of modules=2 (2x3 LED); Operating temperature :=-25 +50 °C; Operating temperature:=-25 +40 °C; Optic=WIDE; Optic :=Metallized polycarbonate reflector; Optic Maintenance=Not available; Optic and illuminating features=-; Overvoltage protection=DM 10KV / CM 10KV; Photobiological Risk Class=RG0; Rated frequency (Hz)=50 / 60; SEO=Street lighting; Shield type=4mm thick flat tempered glass; Standard Deviation Colour Matching=SDCM = 5; Standard-=EN 60598-2-3, EN 60598-1 IEC/TR 62778; Standards and approvals=-; Stocking temperature=-; Supply voltage=220 - 240 V; System power=36W; System power :=38 W @ 0.5A; Tilt adjustable=-20° ÷ +10° side bracket - -10° ÷ +20° pole head; Tilt-=-20° ÷ +10° side bracket - -10° ÷ +20° pole head; Tipologia=Dimmable; Type of light source=LED - Not replaceable; Unified Glare Rating=G*3 - ULOR = 0; Unique digital code (Datamatrix)=Currently not present; Voltage-=220/240 V - 50/60 Hz - Dimmable 1-10 V; Weight (kg):=6,6; Wiring=Isolating switch
- GWR5272M - ROAD5 MINI WIDE 2M 4000K 0,7A CL2 1-10V: Catalogue Range=ROAD [5]; Colour temperature=4000 K (CRI 70); Colour temperature:=4000 K (CRI 70); Descrizione=ROAD 5 MINI DIMM.2M 4000K 700mA OPT.W; EAN code=8011564857902; Electrocod=244C; LED LifeTime (L80B05)=77000H; LED current.=0,7A; Lamp-=LED; Lumen output (lm)=5240; Maximum surface exposed to the wind=0,15M2; Minimum distance from the illuminated object=1M; Modello=GWR5272M; No. Chorus modules=2 (2x3 LED); Nominal flux (lm)=6240; Number of modules=2 (2x3 LED); Operating temperature:=-25 +50 °C; Optic=W - ULOR: 0%; Overvoltage resistance=12 KV (Common and dfferential mode); Pilot current=0,7A; Power supply operation=Dimmable; SEO=Street lighting; System power=53W; Tilt adjustable=-20° ÷ +10° side bracket - -10° ÷ +20° pole head; Tipo alimentatore=Constant Current Driver Led; Tipologia=Dimmable; Type of lamp=LED; Voltage-=220/240 V - 50/60 Hz - Dimmable 1-10 V; Weight (kg)=6,6; Weight (kg):=6,6; Working temperature=-25 +50 °C
- GWR5271B30K - ROAD5 MINI WIDE 1M 3000K 0,7A CL2 BIREG: Body=Die-cast aluminium -; Catalogue Range=ROAD [5]; Classification:=-; Color Rendering Index=CRI-70; Colore=Graphite grey; Colour :=Powder coating; Colour temperature=3000K; Colour temperature:=3000 K (CRI>80); Context=Street and parking lighting; Control System=Bi-power with self-learning; DIN 18032-3 certification=-; Descrizione=GWR5271B30K - ROAD5 MINI WIDE 1M 3000K 0,7A CL2 BIREG; Device with reduced surface temperature=-; Driver=Included; Driver Box=Built-in; Efficiency (lm/W)=100; Electrocod=244C; Eletrical and lighting features=-; External screw=Stainless steel; Fixing=Pole Head - Outreach; Gasket=Anti-aging silicone; General information=-; Glow Wire Test :=-; IPEA=ROAD = A ++ // LARGE AREAS = A3 + // CYCLOPEDONALS = A ++ // GREEN AREAS = A ++ // HISTORICAL CENTER = A5 +; Installationa and maintenance=-; LED Life Time (L80B05)=77000H; LED Maintenance=Not available; LED current.=0,7A; Lamp-=LED; Lifetime=L90B10 (Tq+25°C) = 100.000 h - L90B10 (Tq+50°C) = 75.000 h; Locking Hook=Integrated front handle; Lumen output (lm)=2800; Luminaire=LED Road Equipment; Materials=-; Maximum surface exposed to the wind=0,149999999999999M2; Maximum surface exposed to the wind :=0.15 m²; Minimum distance from the illuminated object=1M; Modello=GWR5271B30K; Mouting and installation=Pole Head - Outreach; Nominal flux (lm)=2700; Number of modules=1 (1x3 LED); Operating temperature :=-25 +50 °C; Operating temperature:=-25 +50 °C; Optic=WIDE; Optic :=Metallized polycarbonate reflector; Optic Maintenance=Not available; Optic and illuminating features=-; Overvoltage protection=DM 10KV / CM 10KV; Overvoltage resistance :=Common and dfferential mode: 10KV; Photobiological Risk Class=RG0; Power supply operation=Bi power; Rated frequency (Hz)=50 / 60; SEO=Street lighting; Shield type=4mm thick flat tempered glass; Standard Deviation Colour Matching=SDCM = 5; Standard-=EN 60598-2-3, EN 60598-1 IEC/TR 62778; Standards and approvals=-; Stocking temperature=-; Supply voltage=220 - 240 V; System power=28W; System power :=28 W @ 0.7A; Tilt adjustable=-20° ÷ +10° side bracket - -10° ÷ +20° pole head; Tilt-=-20° ÷ +10° side bracket - -10° ÷ +20° pole head; Tipo alimentatore=Constant Current Driver Led; Tipologia=Bi power; Type of light source=LED - Not replaceable; Unified Glare Rating=G*3 - ULOR = 0; Unique digital code (Datamatrix)=Currently not present; Voltage-=220/240 V - 50/60 Hz - Bi-power with self-learning; Weight (kg):=6,4; Wiring=Isolating switch
- GWR527130K - ROAD5 MINI WIDE 1M 3000K 0,7A CL2: Body=Die-cast aluminium -; Catalogue Range=ROAD [5]; Classification:=-; Color Rendering Index=CRI-70; Colore=Graphite grey; Colour :=Powder coating; Colour temperature=3000K; Colour temperature:=3000 K (CRI>80); Context=Street and parking lighting; Control System=Stand alone; DIN 18032-3 certification=-; Descrizione=GWR527130K - ROAD5 MINI WIDE 1M 3000K 0,7A CL2; Device with reduced surface temperature=-; Driver=Included; Driver Box=Built-in; Efficiency (lm/W)=104; Electrocod=244C; Eletrical and lighting features=-; External screw=Stainless steel; Fixing=Pole Head - Outreach; Gasket=Anti-aging silicone; General information=-; Glow Wire Test :=-; IPEA=ROAD = A3 + // LARGE AREAS = A3 + // CYCLOPEDONALS = A ++ // GREEN AREAS = A ++ // HISTORICAL CENTER = A6 +; Installationa and maintenance=-; LED Life Time (L80B05)=77000H; LED Maintenance=Not available; LED current.=0,7A; Lamp-=LED; Lifetime=L90B10 (Tq+25°C) = 100.000 h - L90B10 (Tq+50°C) = 75.000 h; Locking Hook=Integrated front handle; Lumen output (lm)=2800; Luminaire=LED Road Equipment; Materials=-; Maximum surface exposed to the wind=0,149999999999999M2; Maximum surface exposed to the wind :=0.15 m²; Minimum distance from the illuminated object=1M; Modello=GWR527130K; Mouting and installation=Pole Head - Outreach; Nominal flux (lm)=2700; Number of modules=1 (1x3 LED); Operating temperature :=-25 +50 °C; Operating temperature:=-25 +40 °C; Optic=WIDE; Optic :=Metallized polycarbonate reflector; Optic Maintenance=Not available; Optic and illuminating features=-; Overvoltage protection=DM 10KV / CM 10KV; Overvoltage resistance :=Common and dfferential mode: 10KV; Photobiological Risk Class=RG0; Rated frequency (Hz)=50 / 60; SEO=Street lighting; Shield type=4mm thick flat tempered glass; Standard Deviation Colour Matching=SDCM = 5; Standard-=EN 60598-2-3, EN 60598-1 IEC/TR 62778; Standards and approvals=-; Stocking temperature=-; Supply voltage=220 - 240 V; System power=27W; System power :=27 W @ 0.7A; Tilt adjustable=-20° ÷ +10° side bracket - -10° ÷ +20° pole head; Tilt-=-20° ÷ +10° side bracket - -10° ÷ +20° pole head; Tipo alimentatore=Constant Current Driver Led; Tipologia=Stand alone; Type of light source=LED - Not replaceable; Unified Glare Rating=G*3 - ULOR = 0; Unique digital code (Datamatrix)=Currently not present; Voltage-=220/240 V - 50/60 Hz - Stand alone; Weight (kg):=6,4; Wiring=Isolating switch
- GWR5211M - ROAD 5 MINI DIMM.1M 4000K 1A OPT.W: Catalogue Range=ROAD [5]; Colour temperature=4000 K (CRI 70); Colour temperature:=4000 K (CRI 70); Descrizione=ROAD 5 MINI DIMM.1M 4000K 1A OPT.W; EAN code=8011564857896; Electrocod=244C; LED LifeTime (L80B05)=120000H; LED current.=1A; Lamp-=LED; Lumen output (lm)=3840; Maximum surface exposed to the wind=0,15M2; Minimum distance from the illuminated object=1M; Modello=GWR5211M; No. Chorus modules=1 (1x3 LED); Nominal flux (lm)=4770; Number of modules=1 (1x3 LED); Operating temperature:=-25 +40 °C; Optic=W - ULOR: 0%; Overvoltage resistance=12 KV (Common and dfferential mode); Pilot current=1A; Power supply operation=Dimmable; SEO=Street lighting; System power=38W; Tilt adjustable=-20° ÷ +10° side bracket - -10° ÷ +20° pole head; Tipo alimentatore=Constant Current Driver Led; Tipologia=Dimmable; Type of lamp=LED; Voltage-=220/240 V - 50/60 Hz - Dimmable 1-10 V; Weight (kg)=6,4; Weight (kg):=6,4; Working temperature=-25 +40 °C
- GWR5252D - ROAD5 MINI WIDE 2M 4000K 0,5A CL2 DALI: Body=Die-cast aluminium -; Classification:=-; Color Rendering Index=CRI-70; Colore=Graphite grey; Colour :=Powder coating; Colour temperature=4000K; Context=Street and parking lighting; Control System=DALI; DIN 18032-3 certification=-; Descrizione=GWR5252D - ROAD5 MINI WIDE 2M 4000K 0,5A CL2 DALI; Device with reduced surface temperature=-; Driver=Included; Driver Box=Built-in; Efficiency (lm/W)=124; Eletrical and lighting features=-; External screw=Stainless steel; Fixing=Pole Head - Outreach; Gasket=Anti-aging silicone; General information=-; Glow Wire Test :=-; IPEA=ROAD = A5 + // LARGE AREAS = A6 + // CYCLOPEDONALS = A5 + // GREEN AREAS = A5 + // HISTORICAL CENTER = A6 +; Installationa and maintenance=-; LED Maintenance=Not available; Lifetime=L90B10 (Tq+25°C) = 100.000 h - L90B10 (Tq+50°C) = 75.000 h; Locking Hook=Integrated front handle; Lumen output (lm)=4700; Luminaire=LED Road Equipment; Materials=-; Maximum surface exposed to the wind :=0.15 m²; Modello=GWR5252D; Mouting and installation=Pole Head - Outreach; Number of modules=2 (2x3 LED); Operating temperature :=-25 +50 °C; Optic=WIDE; Optic :=Metallized polycarbonate reflector; Optic Maintenance=Not available; Optic and illuminating features=-; Overvoltage protection=DM 10KV / CM 10KV; Photobiological Risk Class=RG0; Rated frequency (Hz)=50 / 60; SEO=Street lighting; Shield type=4mm thick flat tempered glass; Standard Deviation Colour Matching=SDCM = 5; Standard-=EN 60598-2-3, EN 60598-1 IEC/TR 62778; Standards and approvals=-; Stocking temperature=-; Supply voltage=220 - 240 V; System power :=38 W @ 0.5A; Tilt-=-20° ÷ +10° side bracket - -10° ÷ +20° pole head; Type of light source=LED - Not replaceable; Unified Glare Rating=G*3 - ULOR = 0; Unique digital code (Datamatrix)=Currently not present; Weight (kg):=6,59999999999999; Wiring=Isolating switch
- GWR5252D30K - ROAD5 MINI WIDE 2M 3000K 0,50A CL2 DALI: Body=Die-cast aluminium -; Classification:=-; Color Rendering Index=CRI-70; Colore=Graphite grey; Colour :=Powder coating; Colour temperature=3000K; Context=Street and parking lighting; Control System=DALI; DIN 18032-3 certification=-; Descrizione=GWR5252D30K - ROAD5 MINI WIDE 2M 3000K 0,50A CL2 DALI; Device with reduced surface temperature=-; Driver=Included; Driver Box=Built-in; Efficiency (lm/W)=108; Eletrical and lighting features=-; External screw=Stainless steel; Fixing=Pole Head - Outreach; Gasket=Anti-aging silicone; General information=-; Glow Wire Test :=-; IPEA=ROAD = A3 + // LARGE AREAS = A4 + // CYCLOPEDONALS = A3 + // GREEN AREAS = A3 + // HISTORICAL CENTER = A6 +; Installationa and maintenance=-; LED Maintenance=Not available; Lifetime=L90B10 (Tq+25°C) = 100.000 h - L90B10 (Tq+50°C) = 75.000 h; Locking Hook=Integrated front handle; Lumen output (lm)=4100; Luminaire=LED Road Equipment; Materials=-; Maximum surface exposed to the wind :=0.15 m²; Modello=GWR5252D30K; Mouting and installation=Pole Head - Outreach; Number of modules=2 (2x3 LED); Operating temperature :=-25 +50 °C; Optic=WIDE; Optic :=Metallized polycarbonate reflector; Optic Maintenance=Not available; Optic and illuminating features=-; Overvoltage protection=DM 10KV / CM 10KV; Photobiological Risk Class=RG0; Rated frequency (Hz)=50 / 60; SEO=Street lighting; Shield type=4mm thick flat tempered glass; Standard Deviation Colour Matching=SDCM = 5; Standard-=EN 60598-2-3, EN 60598-1 IEC/TR 62778; Standards and approvals=-; Stocking temperature=-; Supply voltage=220 - 240 V; System power :=38 W @ 0.5A; Tilt-=-20° ÷ +10° side bracket - -10° ÷ +20° pole head; Type of light source=LED - Not replaceable; Unified Glare Rating=G*3 - ULOR = 0; Unique digital code (Datamatrix)=Currently not present; Weight (kg):=6,59999999999999; Wiring=Isolating switch
- GWR521130K - ROAD 5 MINI ST.AL.1M 3000K 1A OPT.W: Body=Die-cast aluminium -; Catalogue Range=ROAD [5]; Classification:=-; Color Rendering Index=CRI-70; Colore=Graphite grey; Colour :=Powder coating; Colour temperature=3000K; Colour temperature:=3000 K (CRI>80); Context=Street and parking lighting; Control System=Stand alone; DIN 18032-3 certification=-; Descrizione=GWR521130K - ROAD 5 MINI ST.AL.1M 3000K 1A OPT.W; Device with reduced surface temperature=-; Driver=Included; Driver Box=Built-in; Efficiency (lm/W)=97; Electrocod=244C; Eletrical and lighting features=-; External screw=Stainless steel; Fixing=Pole Head - Outreach; Gasket=Anti-aging silicone; General information=-; Glow Wire Test :=-; IPEA=ROAD = A ++ // LARGE AREAS = A ++ // CYCLOPEDONALS = A + // GREEN AREAS = A + // HISTORICAL CENTER = A5 +; Installationa and maintenance=-; LED Life Time (L80B05)=120000H; LED Maintenance=Not available; LED current.=1A; Lamp-=LED; Lifetime=L90B10 (Tq+25°C) = 100.000 h - L90B10 (Tq+40°C) = 75.000 h; Locking Hook=Integrated front handle; Lumen output (lm)=3700; Luminaire=LED Road Equipment; Materials=-; Maximum surface exposed to the wind=0,149999999999999M2; Maximum surface exposed to the wind :=0.15 m²; Minimum distance from the illuminated object=1M; Modello=GWR521130K; Mouting and installation=Pole Head - Outreach; Nominal flux (lm)=4140; Number of modules=1 (1x3 LED); Operating temperature :=-25 +40 °C; Operating temperature:=-25 +40 °C; Optic=WIDE; Optic :=Metallized polycarbonate reflector; Optic Maintenance=Not available; Optic and illuminating features=-; Overvoltage protection=DM 10KV / CM 10KV; Overvoltage resistance :=Common and dfferential mode: 10KV; Photobiological Risk Class=RG0; Rated frequency (Hz)=50 / 60; SEO=Street lighting; Shield type=4mm thick flat tempered glass; Standard Deviation Colour Matching=SDCM = 5; Standard-=EN 60598-2-3, EN 60598-1 IEC/TR 62778; Standards and approvals=-; Stocking temperature=-; Supply voltage=220 - 240 V; System power=38W; System power :=38 W @ 1A; Tilt adjustable=-20° ÷ +10° side bracket - -10° ÷ +20° pole head; Tilt-=-20° ÷ +10° side bracket - -10° ÷ +20° pole head; Tipo alimentatore=Constant Current Driver Led; Tipologia=Stand alone; Type of light source=LED - Not replaceable; Unified Glare Rating=G*3 - ULOR = 0; Unique digital code (Datamatrix)=Currently not present; Voltage-=220/240 V - 50/60 Hz - Stand alone; Weight (kg):=6,4; Wiring=Isolating switch
- GWR5271B - ROAD5 MINI WIDE 1M 4000K 0,7A CL2 BIREG: Catalogue Range=ROAD [5]; Colour temperature=4000 K (CRI 70); Colour temperature:=4000 K (CRI 70); Descrizione=ROAD 5 MINI BIPOW.1M 4000K 700mA OPT.W; EAN code=8011564857841; Electrocod=244C; LED LifeTime (L80B05)=77000H; LED current.=0,7A; Lamp-=LED; Lumen output (lm)=2620; Maximum surface exposed to the wind=0,15M2; Minimum distance from the illuminated object=1M; Modello=GWR5271B; No. Chorus modules=1 (1x3 LED); Nominal flux (lm)=3120; Number of modules=1 (1x3 LED); Operating temperature:=-25 +50 °C; Optic=W - ULOR: 0%; Overvoltage resistance=12 KV (Common and dfferential mode); Pilot current=0,7A; Power supply operation=Bi power; SEO=Street lighting; System power=28W; Tilt adjustable=-20° ÷ +10° side bracket - -10° ÷ +20° pole head; Tipo alimentatore=Constant Current Driver Led; Tipologia=Bi power; Type of lamp=LED; Voltage-=220/240 V - 50/60 Hz - Bi-power with self-learning; Weight (kg)=6,4; Weight (kg):=6,4; Working temperature=-25 +50 °C
- GWR5211D30K - ROAD5 MINI WIDE 1M 3000K 1,0A CL2 DALI: Body=Die-cast aluminium -; Classification:=-; Color Rendering Index=CRI-70; Colore=Graphite grey; Colour :=Powder coating; Colour temperature=3000K; Context=Street and parking lighting; Control System=DALI; DIN 18032-3 certification=-; Descrizione=GWR5211D30K - ROAD5 MINI WIDE 1M 3000K 1,0A CL2 DALI; Device with reduced surface temperature=-; Driver=Included; Driver Box=Built-in; Efficiency (lm/W)=95; Eletrical and lighting features=-; External screw=Stainless steel; Fixing=Pole Head - Outreach; Gasket=Anti-aging silicone; General information=-; Glow Wire Test :=-; IPEA=ROAD = A + // LARGE AREAS = A ++ // CYCLOPEDONALS = A + // GREEN AREAS = A + // HISTORICAL CENTER = A4 +; Installationa and maintenance=-; LED Maintenance=Not available; Lifetime=L90B10 (Tq+25°C) = 100.000 h - L90B10 (Tq+40°C) = 75.000 h; Locking Hook=Integrated front handle; Lumen output (lm)=3700; Luminaire=LED Road Equipment; Materials=-; Maximum surface exposed to the wind :=0.15 m²; Modello=GWR5211D30K; Mouting and installation=Pole Head - Outreach; Number of modules=1 (1x3 LED); Operating temperature :=-25 +40 °C; Optic=WIDE; Optic :=Metallized polycarbonate reflector; Optic Maintenance=Not available; Optic and illuminating features=-; Overvoltage protection=DM 10KV / CM 10KV; Photobiological Risk Class=RG0; Rated frequency (Hz)=50 / 60; Shield type=4mm thick flat tempered glass; Standard Deviation Colour Matching=SDCM = 5; Standard-=EN 60598-2-3, EN 60598-1 IEC/TR 62778; Standards and approvals=-; Stocking temperature=-; Supply voltage=220 - 240 V; System power :=39 W @ 1A; Tilt-=-20° ÷ +10° side bracket - -10° ÷ +20° pole head; Type of light source=LED - Not replaceable; Unified Glare Rating=G*3 - ULOR = 0; Unique digital code (Datamatrix)=Currently not present; Weight (kg):=6,4; Wiring=Isolating switch
- GWR5272V - ROAD5 MINI V.WIDE 2M 4000K 0,7A CL2: Body=Die-cast aluminium -; Catalogue Range=ROAD [5]; Classification:=-; Color Rendering Index=CRI-70; Colore=Graphite grey; Colour :=Powder coating; Colour temperature=4000K; Colour temperature:=4000 K (CRI>70); Context=Street and parking lighting; Control System=DALI - 5 Step; DIN 18032-3 certification=-; Descrizione=GWR5272V - ROAD5 MINI V.WIDE 2M 4000K 0,7A CL2; Device with reduced surface temperature=-; Driver=Included; Driver Box=Built-in; Efficiency (lm/W)=119; Electrocod=244C; Eletrical and lighting features=-; External screw=Stainless steel; Fixing=Pole Head - Outreach; Gasket=Anti-aging silicone; General information=-; Glow Wire Test :=-; IPEA=ROAD = A5 + // LARGE AREAS = A5 + // CYCLOPEDONALS = A4 + // GREEN AREAS = A4 + // HISTORICAL CENTER = A6 +; Installationa and maintenance=-; LED Life Time (L80B05)=77000H; LED Maintenance=Not available; LED current.=0,7A; Lamp-=LED; Lifetime=L90B10 (Tq+25°C) = 100.000 h - L90B10 (Tq+50°C) = 75.000 h; Locking Hook=Integrated front handle; Lumen output (lm)=6400; Luminaire=LED Road Equipment; Materials=-; Maximum surface exposed to the wind=0,149999999999999M2; Maximum surface exposed to the wind :=0.15 m²; Minimum distance from the illuminated object=1M; Modello=GWR5272V; Mouting and installation=Pole Head - Outreach; Nominal flux (lm)=6240; Number of modules=2 (2x3 LED); Operating temperature :=-25 +50 °C; Operating temperature:=-25 +40 °C; Optic=WIDE; Optic :=Metallized polycarbonate reflector; Optic Maintenance=Not available; Optic and illuminating features=-; Overvoltage protection=DM 10KV / CM 10KV; Photobiological Risk Class=RG0; Rated frequency (Hz)=50 / 60; SEO=Street lighting; Shield type=4mm thick flat tempered glass; Standard Deviation Colour Matching=SDCM = 5; Standard-=EN 60598-2-3, EN 60598-1 IEC/TR 62778; Standards and approvals=-; Stocking temperature=-; Supply voltage=220 - 240 V; System power=53W; System power :=54 W @ 0.7A; Tilt adjustable=-20° ÷ +10° side bracket - -10° ÷ +20° pole head; Tilt-=-20° ÷ +10° side bracket - -10° ÷ +20° pole head; Tipologia=Programmable (5 step); Type of light source=LED - Not replaceable; Unified Glare Rating=G*3 - ULOR = 0; Unique digital code (Datamatrix)=Currently not present; Voltage-=220/240 V - 50/60 Hz - Stand alone and/or programmable; Weight (kg):=6,6; Wiring=Isolating switch
- GWR5211V - ROAD5 MINI V.WIDE 1M 4000K 1,0A CL2: Body=Die-cast aluminium -; Catalogue Range=ROAD [5]; Classification:=-; Color Rendering Index=CRI-70; Colore=Graphite grey; Colour :=Powder coating; Colour temperature=4000K; Colour temperature:=4000 K (CRI>70); Context=Street and parking lighting; Control System=DALI - 5 Step; DIN 18032-3 certification=-; Descrizione=GWR5211V - ROAD5 MINI V.WIDE 1M 4000K 1,0A CL2; Device with reduced surface temperature=-; Driver=Included; Driver Box=Built-in; Efficiency (lm/W)=110; Electrocod=244C; Eletrical and lighting features=-; External screw=Stainless steel; Fixing=Pole Head - Outreach; Gasket=Anti-aging silicone; General information=-; Glow Wire Test :=-; IPEA=ROAD = A4 + // LARGE AREAS = A4 + // CYCLOPEDONALS = A3 + // GREEN AREAS = A3 + // HISTORICAL CENTER = A6 +; Installationa and maintenance=-; LED Life Time (L80B05)=120000H; LED Maintenance=Not available; LED current.=1A; Lamp-=LED; Lifetime=L90B10 (Tq+25°C) = 100.000 h - L90B10 (Tq+40°C) = 75.000 h; Locking Hook=Integrated front handle; Lumen output (lm)=4300; Luminaire=LED Road Equipment; Materials=-; Maximum surface exposed to the wind=0,149999999999999M2; Maximum surface exposed to the wind :=0.15 m²; Minimum distance from the illuminated object=1M; Modello=GWR5211V; Mouting and installation=Pole Head - Outreach; Nominal flux (lm)=4770; Number of modules=1 (1x3 LED); Operating temperature :=-25 +40 °C; Operating temperature:=-25 +40 °C; Optic=WIDE; Optic :=Metallized polycarbonate reflector; Optic Maintenance=Not available; Optic and illuminating features=-; Overvoltage protection=DM 10KV / CM 10KV; Photobiological Risk Class=RG0; Rated frequency (Hz)=50 / 60; SEO=Street lighting; Shield type=4mm thick flat tempered glass; Standard Deviation Colour Matching=SDCM = 5; Standard-=EN 60598-2-3, EN 60598-1 IEC/TR 62778; Standards and approvals=-; Stocking temperature=-; Supply voltage=220 - 240 V; System power=38W; System power :=39 W @ 1A; Tilt adjustable=-20° ÷ +10° side bracket - -10° ÷ +20° pole head; Tilt-=-20° ÷ +10° side bracket - -10° ÷ +20° pole head; Tipologia=Programmable (5 step); Type of light source=LED - Not replaceable; Unified Glare Rating=G*3 - ULOR = 0; Unique digital code (Datamatrix)=Currently not present; Voltage-=220/240 V - 50/60 Hz - Stand alone and/or programmable; Weight (kg):=6,4; Wiring=Isolating switch
- GWR5251D - ROAD5 MINI WIDE 1M 4000K 0,5A CL2 DALI: Body=Die-cast aluminium -; Classification:=-; Color Rendering Index=CRI-70; Colore=Graphite grey; Colour :=Powder coating; Colour temperature=4000K; Context=Street and parking lighting; Control System=DALI; DIN 18032-3 certification=-; Descrizione=GWR5251D - ROAD5 MINI WIDE 1M 4000K 0,5A CL2 DALI; Device with reduced surface temperature=-; Driver=Included; Driver Box=Built-in; Efficiency (lm/W)=120; Eletrical and lighting features=-; External screw=Stainless steel; Fixing=Pole Head - Outreach; Gasket=Anti-aging silicone; General information=-; Glow Wire Test :=-; IPEA=ROAD = A5 + // LARGE AREAS = A6 + // CYCLOPEDONALS = A5 + // GREEN AREAS = A5 + // HISTORICAL CENTER = A6 +; Installationa and maintenance=-; LED Maintenance=Not available; Lifetime=L90B10 (Tq+25°C) = 100.000 h - L90B10 (Tq+50°C) = 75.000 h; Locking Hook=Integrated front handle; Lumen output (lm)=2400; Luminaire=LED Road Equipment; Materials=-; Maximum surface exposed to the wind :=0.15 m²; Modello=GWR5251D; Mouting and installation=Pole Head - Outreach; Number of modules=1 (1x3 LED); Operating temperature :=-25 +50 °C; Optic=WIDE; Optic :=Metallized polycarbonate reflector; Optic Maintenance=Not available; Optic and illuminating features=-; Overvoltage protection=DM 10KV / CM 10KV; Photobiological Risk Class=RG0; Rated frequency (Hz)=50 / 60; Shield type=4mm thick flat tempered glass; Standard Deviation Colour Matching=SDCM = 5; Standard-=EN 60598-2-3, EN 60598-1 IEC/TR 62778; Standards and approvals=-; Stocking temperature=-; Supply voltage=220 - 240 V; System power :=20 W @ 0.5A; Tilt-=-20° ÷ +10° side bracket - -10° ÷ +20° pole head; Type of light source=LED - Not replaceable; Unified Glare Rating=G*3 - ULOR = 0; Unique digital code (Datamatrix)=Currently not present; Weight (kg):=6,4; Wiring=Isolating switch
- GWR5212M30K - ROAD5 MINI WIDE 2M 3000K 1,0A CL2 1-10V: Body=Die-cast aluminium -; Catalogue Range=ROAD [5]; Classification:=-; Color Rendering Index=CRI-70; Colore=Graphite grey; Colour :=Powder coating; Colour temperature=3000K; Colour temperature:=3000 K (CRI>80); Context=Street and parking lighting; Control System=Dimmable 1-10 V; DIN 18032-3 certification=-; Descrizione=GWR5212M30K - ROAD5 MINI WIDE 2M 3000K 1,0A CL2 1-10V; Device with reduced surface temperature=-; Driver=Included; Driver Box=Built-in; Efficiency (lm/W)=96; Electrocod=244C; Eletrical and lighting features=-; External screw=Stainless steel; Fixing=Pole Head - Outreach; Gasket=Anti-aging silicone; General information=-; Glow Wire Test :=-; IPEA=ROAD = A + // LARGE AREAS = A ++ // CYCLOPEDONALS = A + // GREEN AREAS = A + // HISTORICAL CENTER = A5 +; Installationa and maintenance=-; LED Life Time (L80B05)=120000H; LED Maintenance=Not available; LED current.=1A; Lamp-=LED; Lifetime=L90B10 (Tq+25°C) = 100.000 h - L90B10 (Tq+40°C) = 75.000 h; Locking Hook=Integrated front handle; Lumen output (lm)=7400; Luminaire=LED Road Equipment; Materials=-; Maximum surface exposed to the wind=0,149999999999999M2; Maximum surface exposed to the wind :=0.15 m²; Minimum distance from the illuminated object=1M; Modello=GWR5212M30K; Mouting and installation=Pole Head - Outreach; Nominal flux (lm)=8280; Number of modules=2 (2x3 LED); Operating temperature :=-25 +40 °C; Operating temperature:=-25 +40 °C; Optic=WIDE; Optic :=Metallized polycarbonate reflector; Optic Maintenance=Not available; Optic and illuminating features=-; Overvoltage protection=DM 10KV / CM 10KV; Overvoltage resistance :=Common and dfferential mode: 10KV; Photobiological Risk Class=RG0; Power supply operation=Dimmable; Rated frequency (Hz)=50 / 60; SEO=Street lighting; Shield type=4mm thick flat tempered glass; Standard Deviation Colour Matching=SDCM = 5; Standard-=EN 60598-2-3, EN 60598-1 IEC/TR 62778; Standards and approvals=-; Stocking temperature=-; Supply voltage=220 - 240 V; System power=76W; System power :=77 W @ 1A; Tilt adjustable=-20° ÷ +10° side bracket - -10° ÷ +20° pole head; Tilt-=-20° ÷ +10° side bracket - -10° ÷ +20° pole head; Tipo alimentatore=Constant Current Driver Led; Tipologia=Dimmable; Type of light source=LED - Not replaceable; Unified Glare Rating=G*3 - ULOR = 0; Unique digital code (Datamatrix)=Currently not present; Voltage-=220/240 V - 50/60 Hz - Dimmable 1-10 V; Weight (kg):=6,6; Wiring=Isolating switch
- GWR5211M30K - ROAD 5 MINI DIMM.1M 3000K 1A OPT.W: Body=Die-cast aluminium -; Catalogue Range=ROAD [5]; Classification:=-; Color Rendering Index=CRI-70; Colore=Graphite grey; Colour :=Powder coating; Colour temperature=3000K; Colour temperature:=3000 K (CRI>80); Context=Street and parking lighting; Control System=Dimmable 1-10 V; DIN 18032-3 certification=-; Descrizione=GWR5211M30K - ROAD 5 MINI DIMM.1M 3000K 1A OPT.W; Device with reduced surface temperature=-; Driver=Included; Driver Box=Built-in; Efficiency (lm/W)=95; Electrocod=244C; Eletrical and lighting features=-; External screw=Stainless steel; Fixing=Pole Head - Outreach; Gasket=Anti-aging silicone; General information=-; Glow Wire Test :=-; IPEA=ROAD = A + // LARGE AREAS = A ++ // CYCLOPEDONALS = A + // GREEN AREAS = A + // HISTORICAL CENTER = A4 +; Installationa and maintenance=-; LED Life Time (L80B05)=120000H; LED Maintenance=Not available; LED current.=1A; Lamp-=LED; Lifetime=L90B10 (Tq+25°C) = 100.000 h - L90B10 (Tq+40°C) = 75.000 h; Locking Hook=Integrated front handle; Lumen output (lm)=3700; Luminaire=LED Road Equipment; Materials=-; Maximum surface exposed to the wind=0,149999999999999M2; Maximum surface exposed to the wind :=0.15 m²; Minimum distance from the illuminated object=1M; Modello=GWR5211M30K; Mouting and installation=Pole Head - Outreach; Nominal flux (lm)=4140; Number of modules=1 (1x3 LED); Operating temperature :=-25 +40 °C; Operating temperature:=-25 +40 °C; Optic=WIDE; Optic :=Metallized polycarbonate reflector; Optic Maintenance=Not available; Optic and illuminating features=-; Overvoltage protection=DM 10KV / CM 10KV; Overvoltage resistance :=Common and dfferential mode: 10KV; Photobiological Risk Class=RG0; Power supply operation=Dimmable; Rated frequency (Hz)=50 / 60; SEO=Street lighting; Shield type=4mm thick flat tempered glass; Standard Deviation Colour Matching=SDCM = 5; Standard-=EN 60598-2-3, EN 60598-1 IEC/TR 62778; Standards and approvals=-; Stocking temperature=-; Supply voltage=220 - 240 V; System power=38W; System power :=39 W @ 1A; Tilt adjustable=-20° ÷ +10° side bracket - -10° ÷ +20° pole head; Tilt-=-20° ÷ +10° side bracket - -10° ÷ +20° pole head; Tipo alimentatore=Constant Current Driver Led; Tipologia=Dimmable; Type of light source=LED - Not replaceable; Unified Glare Rating=G*3 - ULOR = 0; Unique digital code (Datamatrix)=Currently not present; Voltage-=220/240 V - 50/60 Hz - Dimmable 1-10 V; Weight (kg):=6,4; Wiring=Isolating switch
- GWR5272M30K - ROAD5 MINI WIDE 2M 3000K 0,7A CL2 1-10V: Body=Die-cast aluminium -; Catalogue Range=ROAD [5]; Classification:=-; Color Rendering Index=CRI-70; Colore=Graphite grey; Colour :=Powder coating; Colour temperature=3000K; Colour temperature:=3000 K (CRI>80); Context=Street and parking lighting; Control System=Dimmable 1-10 V; DIN 18032-3 certification=-; Descrizione=GWR5272M30K - ROAD5 MINI WIDE 2M 3000K 0,7A CL2 1-10V; Device with reduced surface temperature=-; Driver=Included; Driver Box=Built-in; Efficiency (lm/W)=102; Electrocod=244C; Eletrical and lighting features=-; External screw=Stainless steel; Fixing=Pole Head - Outreach; Gasket=Anti-aging silicone; General information=-; Glow Wire Test :=-; IPEA=ROAD = A ++ // LARGE AREAS = A3 + // CYCLOPEDONALS = A ++ // GREEN AREAS = A ++ // HISTORICAL CENTER = A5 +; Installationa and maintenance=-; LED Life Time (L80B05)=77000H; LED Maintenance=Not available; LED current.=0,7A; Lamp-=LED; Lifetime=L90B10 (Tq+25°C) = 100.000 h - L90B10 (Tq+50°C) = 75.000 h; Locking Hook=Integrated front handle; Lumen output (lm)=5500; Luminaire=LED Road Equipment; Materials=-; Maximum surface exposed to the wind=0,149999999999999M2; Maximum surface exposed to the wind :=0.15 m²; Minimum distance from the illuminated object=1M; Modello=GWR5272M30K; Mouting and installation=Pole Head - Outreach; Nominal flux (lm)=5400; Number of modules=2 (2x3 LED); Operating temperature :=-25 +50 °C; Operating temperature:=-25 +50 °C; Optic=WIDE; Optic :=Metallized polycarbonate reflector; Optic Maintenance=Not available; Optic and illuminating features=-; Overvoltage protection=DM 10KV / CM 10KV; Overvoltage resistance :=Common and dfferential mode: 10KV; Photobiological Risk Class=RG0; Power supply operation=Dimmable; Rated frequency (Hz)=50 / 60; SEO=Street lighting; Shield type=4mm thick flat tempered glass; Standard Deviation Colour Matching=SDCM = 5; Standard-=EN 60598-2-3, EN 60598-1 IEC/TR 62778; Standards and approvals=-; Stocking temperature=-; Supply voltage=220 - 240 V; System power=53W; System power :=54 W @ 0.7A; Tilt adjustable=-20° ÷ +10° side bracket - -10° ÷ +20° pole head; Tilt-=-20° ÷ +10° side bracket - -10° ÷ +20° pole head; Tipo alimentatore=Constant Current Driver Led; Tipologia=Dimmable; Type of light source=LED - Not replaceable; Unified Glare Rating=G*3 - ULOR = 0; Unique digital code (Datamatrix)=Currently not present; Voltage-=220/240 V - 50/60 Hz - Dimmable 1-10 V; Weight (kg):=6,6; Wiring=Isolating switch
- GWR5251B - ROAD5 MINI WIDE 1M 4000K 0,5A CL2 BIREG: Body=Die-cast aluminium -; Catalogue Range=ROAD [5]; Classification:=-; Color Rendering Index=CRI-70; Colore=Graphite grey; Colour :=Powder coating; Colour temperature=4000K; Colour temperature:=4000 K (CRI>70); Context=Street and parking lighting; Control System=Bi-power with self-learning; DIN 18032-3 certification=-; Descrizione=GWR5251B - ROAD5 MINI WIDE 1M 4000K 0,5A CL2 BIREG; Device with reduced surface temperature=-; Driver=Included; Driver Box=Built-in; Efficiency (lm/W)=120; Electrocod=244C; Eletrical and lighting features=-; External screw=Stainless steel; Fixing=Pole Head - Outreach; Gasket=Anti-aging silicone; General information=-; Glow Wire Test :=-; IPEA=ROAD = A5 + // LARGE AREAS = A6 + // CYCLOPEDONALS = A5 + // GREEN AREAS = A5 + // HISTORICAL CENTER = A6 +; Installationa and maintenance=-; LED Life Time (L80B05)=120000H; LED Maintenance=Not available; LED current.=0,5A; Lamp-=LED; Lifetime=L90B10 (Tq+25°C) = 100.000 h - L90B10 (Tq+50°C) = 75.000 h; Locking Hook=Integrated front handle; Lumen output (lm)=2400; Luminaire=LED Road Equipment; Materials=-; Maximum surface exposed to the wind=0,149999999999999M2; Maximum surface exposed to the wind :=0.15 m²; Minimum distance from the illuminated object=1M; Modello=GWR5251B; Mouting and installation=Pole Head - Outreach; Nominal flux (lm)=2400; Number of modules=1 (1x3 LED); Operating temperature :=-25 +50 °C; Operating temperature:=-25 +40 °C; Optic=WIDE; Optic :=Metallized polycarbonate reflector; Optic Maintenance=Not available; Optic and illuminating features=-; Overvoltage protection=DM 10KV / CM 10KV; Photobiological Risk Class=RG0; Power supply operation=Bi power; Rated frequency (Hz)=50 / 60; SEO=Street lighting; Shield type=4mm thick flat tempered glass; Standard Deviation Colour Matching=SDCM = 5; Standard-=EN 60598-2-3, EN 60598-1 IEC/TR 62778; Standards and approvals=-; Stocking temperature=-; Supply voltage=220 - 240 V; System power=18W; System power :=20 W @ 0.5A; Tilt adjustable=-20° ÷ +10° side bracket - -10° ÷ +20° pole head; Tilt-=-20° ÷ +10° side bracket - -10° ÷ +20° pole head; Type of light source=LED - Not replaceable; Unified Glare Rating=G*3 - ULOR = 0; Unique digital code (Datamatrix)=Currently not present; Voltage-=220/240 V - 50/60 Hz - Bi-power with self-learning; Weight (kg):=6,4; Wiring=Isolating switch
- GWR521230K - ROAD 5 MINI ST.AL.2M 3000K 1A OPT.W: Body=Die-cast aluminium -; Catalogue Range=ROAD [5]; Classification:=-; Color Rendering Index=CRI-70; Colore=Graphite grey; Colour :=Powder coating; Colour temperature=3000K; Colour temperature:=3000 K (CRI>80); Context=Street and parking lighting; Control System=Stand alone; DIN 18032-3 certification=-; Descrizione=GWR521230K - ROAD 5 MINI ST.AL.2M 3000K 1A OPT.W; Device with reduced surface temperature=-; Driver=Included; Driver Box=Built-in; Efficiency (lm/W)=101; Electrocod=244C; Eletrical and lighting features=-; External screw=Stainless steel; Fixing=Pole Head - Outreach; Gasket=Anti-aging silicone; General information=-; Glow Wire Test :=-; IPEA=ROAD = A ++ // LARGE AREAS = A3 + // CYCLOPEDONALS = A + // GREEN AREAS = A + // HISTORICAL CENTER = A5 +; Installationa and maintenance=-; LED Life Time (L80B05)=120000H; LED Maintenance=Not available; LED current.=0,9A; Lamp-=LED; Lifetime=L90B10 (Tq+25°C) = 100.000 h - L90B10 (Tq+40°C) = 75.000 h; Locking Hook=Integrated front handle; Lumen output (lm)=6800; Luminaire=LED Road Equipment; Materials=-; Maximum surface exposed to the wind=0,149999999999999M2; Maximum surface exposed to the wind :=0.15 m²; Minimum distance from the illuminated object=1M; Modello=GWR521230K; Mouting and installation=Pole Head - Outreach; Nominal flux (lm)=8280; Number of modules=2 (2x3 LED); Operating temperature :=-25 +40 °C; Operating temperature:=-25 +40 °C; Optic=WIDE; Optic :=Metallized polycarbonate reflector; Optic Maintenance=Not available; Optic and illuminating features=-; Overvoltage protection=DM 10KV / CM 10KV; Overvoltage resistance :=Common and dfferential mode: 10KV; Photobiological Risk Class=RG0; Rated frequency (Hz)=50 / 60; SEO=Street lighting; Shield type=4mm thick flat tempered glass; Standard Deviation Colour Matching=SDCM = 5; Standard-=EN 60598-2-3, EN 60598-1 IEC/TR 62778; Standards and approvals=-; Stocking temperature=-; Supply voltage=220 - 240 V; System power=76W; System power :=67 W @ 0.9A; Tilt adjustable=-20° ÷ +10° side bracket - -10° ÷ +20° pole head; Tilt-=-20° ÷ +10° side bracket - -10° ÷ +20° pole head; Tipo alimentatore=Constant Current Driver Led; Tipologia=Stand alone; Type of light source=LED - Not replaceable; Unified Glare Rating=G*3 - ULOR = 0; Unique digital code (Datamatrix)=Currently not present; Voltage-=220/240 V - 50/60 Hz - Stand alone; Weight (kg):=6,6; Wiring=Isolating switch
- GWR5271 - ROAD 5 MINI ST.AL.1M 4000K 700mA OPT.W: Catalogue Range=ROAD [5]; Colour temperature=4000 K (CRI 70); Colour temperature:=4000 K (CRI 70); Descrizione=ROAD 5 MINI ST.AL.1M 4000K 700mA OPT.W; EAN code=8011564857803; Electrocod=244C; LED LifeTime (L80B05)=77000H; LED current.=0,7A; Lamp-=LED; Lumen output (lm)=2620; Maximum surface exposed to the wind=0,15M2; Minimum distance from the illuminated object=1M; Modello=GWR5271; No. Chorus modules=1 (1x3 LED); Nominal flux (lm)=3120; Number of modules=1 (1x3 LED); Operating temperature:=-25 +50 °C; Optic=W - ULOR: 0%; Overvoltage resistance=12 KV (Common and dfferential mode); Pilot current=0,7A; SEO=Street lighting; System power=27W; Tilt adjustable=-20° ÷ +10° side bracket - -10° ÷ +20° pole head; Tipo alimentatore=Constant Current Driver Led; Tipologia=Stand alone; Type of lamp=LED; Voltage-=220/240 V - 50/60 Hz - Stand alone; Weight (kg)=6,4; Weight (kg):=6,4; Working temperature=-25 +50 °C
- GWR5212M - ROAD 5 MINI DIMM.2M 4000K 1A OPT.W: Catalogue Range=ROAD [5]; Colour temperature=4000 K (CRI 70); Colour temperature:=4000 K (CRI 70); Descrizione=ROAD 5 MINI DIMM.2M 4000K 1A OPT.W; EAN code=8011564857919; Electrocod=244C; LED LifeTime (L80B05)=120000H; LED current.=1A; Lamp-=LED; Lumen output (lm)=7680; Maximum surface exposed to the wind=0,15M2; Minimum distance from the illuminated object=1M; Modello=GWR5212M; No. Chorus modules=2 (2x3 LED); Nominal flux (lm)=9540; Number of modules=2 (2x3 LED); Operating temperature:=-25 +40 °C; Optic=W - ULOR: 0%; Overvoltage resistance=12 KV (Common and dfferential mode); Pilot current=1A; Power supply operation=Dimmable; SEO=Street lighting; System power=76W; Tilt adjustable=-20° ÷ +10° side bracket - -10° ÷ +20° pole head; Tipo alimentatore=Constant Current Driver Led; Tipologia=Dimmable; Type of lamp=LED; Voltage-=220/240 V - 50/60 Hz - Dimmable 1-10 V; Weight (kg)=6,6; Weight (kg):=6,6; Working temperature=-25 +40 °C
- GWR5272B - ROAD 5 MINI BIPOW.2M 4000K 700mA OPT.W: Catalogue Range=ROAD [5]; Colour temperature=4000 K (CRI 70); Colour temperature:=4000 K (CRI 70); Descrizione=ROAD 5 MINI BIPOW.2M 4000K 700mA OPT.W; EAN code=8011564857865; Electrocod=244C; LED LifeTime (L80B05)=77000H; LED current.=0,7A; Lamp-=LED; Lumen output (lm)=5240; Maximum surface exposed to the wind=0,15M2; Minimum distance from the illuminated object=1M; Modello=GWR5272B; No. Chorus modules=2 (2x3 LED); Nominal flux (lm)=6240; Number of modules=2 (2x3 LED); Operating temperature:=-25 +50 °C; Optic=W - ULOR: 0%; Overvoltage resistance=12 KV (Common and dfferential mode); Pilot current=0,7A; Power supply operation=Bi power; SEO=Street lighting; System power=54W; Tilt adjustable=-20° ÷ +10° side bracket - -10° ÷ +20° pole head; Tipo alimentatore=Constant Current Driver Led; Tipologia=Bi power; Type of lamp=LED; Voltage-=220/240 V - 50/60 Hz - Bi-power with self-learning; Weight (kg)=6,6; Weight (kg):=6,6; Working temperature=-25 +50 °C
- GWR5251B30K - ROAD5 MINI WIDE 1M 3000K 0,50A CL2 BIREG: Body=Die-cast aluminium -; Classification:=-; Color Rendering Index=CRI-70; Colore=Graphite grey; Colour :=Powder coating; Colour temperature=3000K; Context=Street and parking lighting; Control System=Bi-power with self-learning; DIN 18032-3 certification=-; Descrizione=GWR5251B30K - ROAD5 MINI WIDE 1M 3000K 0,50A CL2 BIREG; Device with reduced surface temperature=-; Driver=Included; Driver Box=Built-in; Efficiency (lm/W)=105; Eletrical and lighting features=-; External screw=Stainless steel; Fixing=Pole Head - Outreach; Gasket=Anti-aging silicone; General information=-; Glow Wire Test :=-; IPEA=ROAD = A3 + // LARGE AREAS = A3 + // CYCLOPEDONALS = A3 + // GREEN AREAS = A3 + // HISTORICAL CENTER = A6 +; Installationa and maintenance=-; LED Maintenance=Not available; Lifetime=L90B10 (Tq+25°C) = 100.000 h - L90B10 (Tq+50°C) = 75.000 h; Locking Hook=Integrated front handle; Lumen output (lm)=2100; Luminaire=LED Road Equipment; Materials=-; Maximum surface exposed to the wind :=0.15 m²; Modello=GWR5251B30K; Mouting and installation=Pole Head - Outreach; Number of modules=1 (1x3 LED); Operating temperature :=-25 +50 °C; Optic=WIDE; Optic :=Metallized polycarbonate reflector; Optic Maintenance=Not available; Optic and illuminating features=-; Overvoltage protection=DM 10KV / CM 10KV; Photobiological Risk Class=RG0; Rated frequency (Hz)=50 / 60; SEO=Street lighting; Shield type=4mm thick flat tempered glass; Standard Deviation Colour Matching=SDCM = 5; Standard-=EN 60598-2-3, EN 60598-1 IEC/TR 62778; Standards and approvals=-; Stocking temperature=-; Supply voltage=220 - 240 V; System power :=20 W @ 0.5A; Tilt-=-20° ÷ +10° side bracket - -10° ÷ +20° pole head; Type of light source=LED - Not replaceable; Unified Glare Rating=G*3 - ULOR = 0; Unique digital code (Datamatrix)=Currently not present; Weight (kg):=6,4; Wiring=Isolating switch
- GWR5251M - ROAD5 MINI WIDE 1M 4000K 0,5A CL2 1-10V: Body=Die-cast aluminium -; Catalogue Range=ROAD [5]; Classification:=-; Color Rendering Index=CRI-70; Colore=Graphite grey; Colour :=Powder coating; Colour temperature=4000K; Colour temperature:=4000 K (CRI>70); Context=Street and parking lighting; Control System=Dimmable 1-10 V; DIN 18032-3 certification=-; Descrizione=GWR5251M - ROAD5 MINI WIDE 1M 4000K 0,5A CL2 1-10V; Device with reduced surface temperature=-; Driver=Included; Driver Box=Built-in; Efficiency (lm/W)=120; Electrocod=244C; Eletrical and lighting features=-; External screw=Stainless steel; Fixing=Pole Head - Outreach; Gasket=Anti-aging silicone; General information=-; Glow Wire Test :=-; IPEA=ROAD = A5 + // LARGE AREAS = A6 + // CYCLOPEDONALS = A5 + // GREEN AREAS = A5 + // HISTORICAL CENTER = A6 +; Installationa and maintenance=-; LED Life Time (L80B05)=120000H; LED Maintenance=Not available; LED current.=0,5A; Lamp-=LED; Lifetime=L90B10 (Tq+25°C) = 100.000 h - L90B10 (Tq+50°C) = 75.000 h; Locking Hook=Integrated front handle; Lumen output (lm)=2400; Luminaire=LED Road Equipment; Materials=-; Maximum surface exposed to the wind=0,149999999999999M2; Maximum surface exposed to the wind :=0.15 m²; Minimum distance from the illuminated object=1M; Modello=GWR5251M; Mouting and installation=Pole Head - Outreach; Nominal flux (lm)=2400; Number of modules=1 (1x3 LED); Operating temperature :=-25 +50 °C; Operating temperature:=-25 +40 °C; Optic=WIDE; Optic :=Metallized polycarbonate reflector; Optic Maintenance=Not available; Optic and illuminating features=-; Overvoltage protection=DM 10KV / CM 10KV; Photobiological Risk Class=RG0; Rated frequency (Hz)=50 / 60; SEO=Street lighting; Shield type=4mm thick flat tempered glass; Standard Deviation Colour Matching=SDCM = 5; Standard-=EN 60598-2-3, EN 60598-1 IEC/TR 62778; Standards and approvals=-; Stocking temperature=-; Supply voltage=220 - 240 V; System power=18W; System power :=20 W @ 0.5A; Tilt adjustable=-20° ÷ +10° side bracket - -10° ÷ +20° pole head; Tilt-=-20° ÷ +10° side bracket - -10° ÷ +20° pole head; Tipologia=Dimmable; Type of light source=LED - Not replaceable; Unified Glare Rating=G*3 - ULOR = 0; Unique digital code (Datamatrix)=Currently not present; Voltage-=220/240 V - 50/60 Hz - Dimmable 1-10 V; Weight (kg):=6,4; Wiring=Isolating switch
